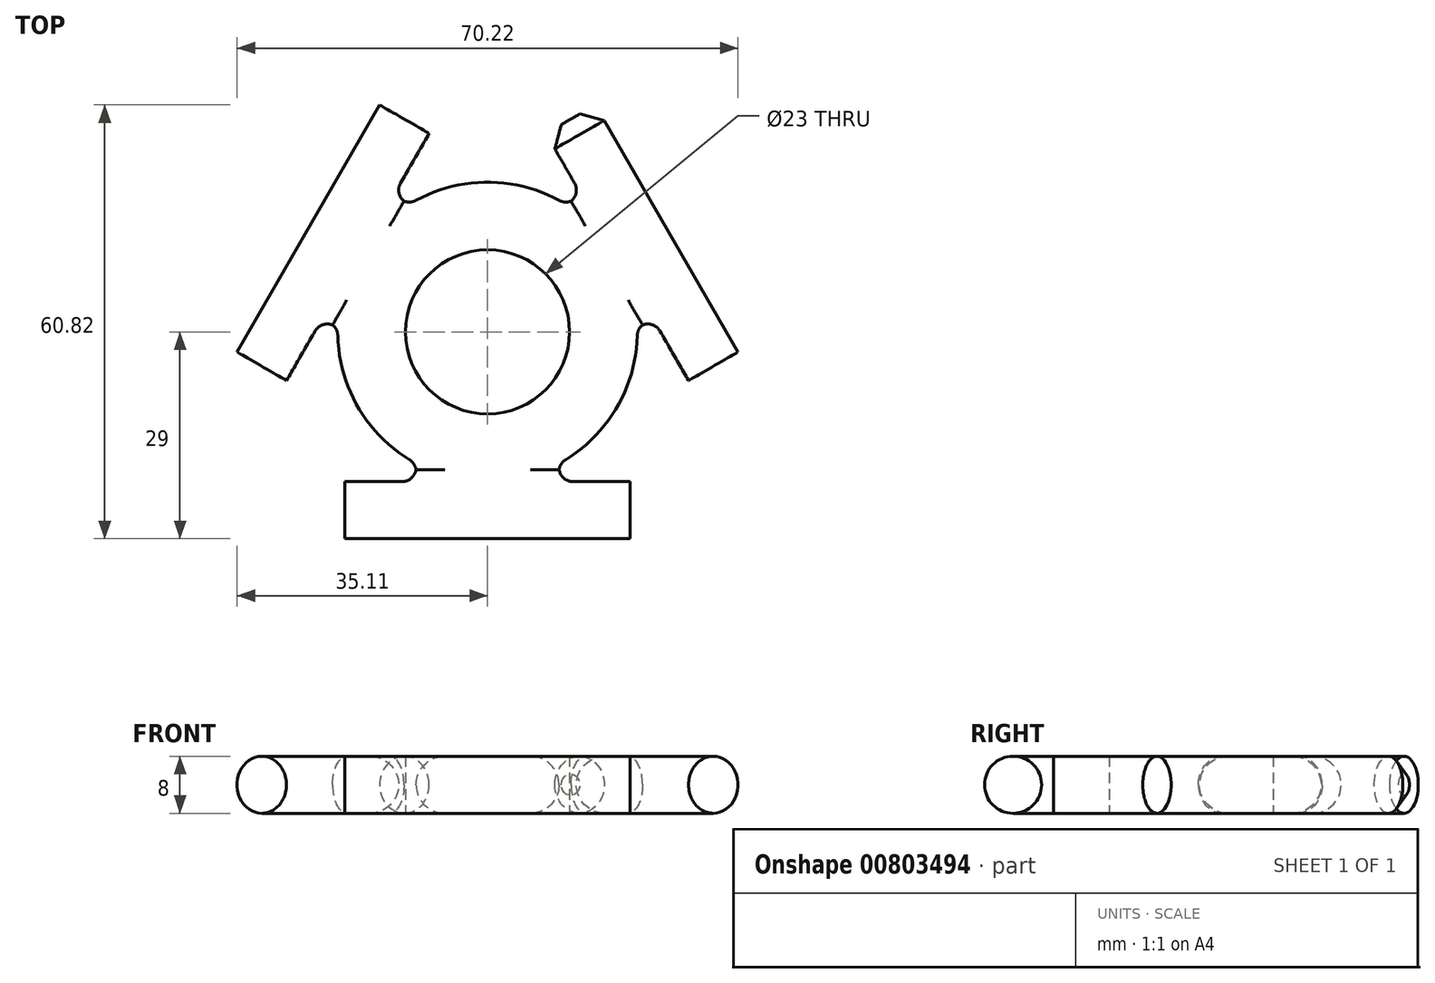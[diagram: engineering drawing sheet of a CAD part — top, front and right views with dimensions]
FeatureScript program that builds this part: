
annotation { "Feature Type Name" : "Feature", "Feature Type Description" : "" }
export const myFeature = defineFeature(function(context is Context, id is Id, definition is map)
    precondition{}
    {
        {
            var Q0;
            Q0=qCreatedBy(makeId("Top.planeOp"),FACE);
            var sketch = newSketch(context, id + "F0", { "sketchPlane" : qUnion([Q0])});
            skLineSegment(sketch, "E0", {"start": v(0, 45.61) * mm, "end": v(0, -48.73) * mm, "construction": true});
            skLineSegment(sketch, "E1", {"start": v(0, -21) * mm, "end": v(-20, -21) * mm});
            skLineSegment(sketch, "E2", {"start": v(-20, -21) * mm, "end": v(-20, -29) * mm});
            skLineSegment(sketch, "E3", {"start": v(-20, -29) * mm, "end": v(0, -29) * mm});
            skLineSegment(sketch, "E4", {"start": v(-20, -25) * mm, "end": v(0, -25) * mm, "construction": true});
            skCircle(sketch, "E5", {"center": v(0, 0) * mm, "radius": 11.5 * mm});
            skCircle(sketch, "E6", {"center": v(0, 0) * mm, "radius": 21 * mm});
            skLineSegment(sketch, "E7.MirrorCS", {"start": v(0, -21) * mm, "end": v(20, -21) * mm});
            skLineSegment(sketch, "E8.MirrorCS", {"start": v(20, -21) * mm, "end": v(20, -29) * mm});
            skLineSegment(sketch, "E9.MirrorCS", {"start": v(20, -29) * mm, "end": v(0, -29) * mm});
            skLineSegment(sketch, "E10", {"start": v(0, 0) * mm, "end": v(46.84, 27.05) * mm, "construction": true});
            skLineSegment(sketch, "E11", {"start": v(0, 0) * mm, "end": v(-46.66, 26.94) * mm, "construction": true});
            skLineSegment(sketch, "E12.1.0", {"start": v(18.19, 10.5) * mm, "end": v(28.19, -6.82) * mm});
            skLineSegment(sketch, "E12.1.1", {"start": v(28.19, -6.82) * mm, "end": v(35.11, -2.82) * mm});
            skLineSegment(sketch, "E12.1.2", {"start": v(35.11, -2.82) * mm, "end": v(25.11, 14.5) * mm});
            skLineSegment(sketch, "E12.1.3", {"start": v(15.11, 31.82) * mm, "end": v(25.11, 14.5) * mm});
            skLineSegment(sketch, "E12.1.4", {"start": v(8.19, 27.82) * mm, "end": v(15.11, 31.82) * mm});
            skLineSegment(sketch, "E12.1.5", {"start": v(18.19, 10.5) * mm, "end": v(8.19, 27.82) * mm});
            skLineSegment(sketch, "E12.2.0", {"start": v(-18.19, 10.5) * mm, "end": v(-8.19, 27.82) * mm});
            skLineSegment(sketch, "E12.2.1", {"start": v(-8.19, 27.82) * mm, "end": v(-15.11, 31.82) * mm});
            skLineSegment(sketch, "E12.2.2", {"start": v(-15.11, 31.82) * mm, "end": v(-25.11, 14.5) * mm});
            skLineSegment(sketch, "E12.2.3", {"start": v(-35.11, -2.82) * mm, "end": v(-25.11, 14.5) * mm});
            skLineSegment(sketch, "E12.2.4", {"start": v(-28.19, -6.82) * mm, "end": v(-35.11, -2.82) * mm});
            skLineSegment(sketch, "E12.2.5", {"start": v(-18.19, 10.5) * mm, "end": v(-28.19, -6.82) * mm});
            skLineSegment(sketch, "E13", {"start": v(-10, -21) * mm, "end": v(-10, -18.47) * mm});
            skLineSegment(sketch, "E14", {"start": v(10, -21) * mm, "end": v(10, -18.47) * mm});
            skLineSegment(sketch, "E15.1.0", {"start": v(13.19, 19.16) * mm, "end": v(11, 17.9) * mm});
            skLineSegment(sketch, "E15.1.1", {"start": v(23.19, 1.84) * mm, "end": v(21, 0.57) * mm});
            skLineSegment(sketch, "E15.2.0", {"start": v(-23.19, 1.84) * mm, "end": v(-21, 0.57) * mm});
            skLineSegment(sketch, "E15.2.1", {"start": v(-13.19, 19.16) * mm, "end": v(-11, 17.9) * mm});
            skSolve(sketch);
        }
        {
            var Q0;
            Q0 = qSketchRegion(id + "F0", true);
            extrude(context, id + "F1", {"entities" : qUnion([Q0]), "depth" : 8 * mm, "offsetDistance" : 25 * mm});
        }
        {
            var Q0;
            Q0=makeQuery(id+"F1.opExtrude","SWEPT_EDGE",EDGE,{"disambiguationData":[OSD([sQuery(id+"F0.wireOp",EDGE,"E6"),sQuery(id+"F0.wireOp",EDGE,"E15.2.1")])]});
            var Q1;
            Q1=makeQuery(id+"F1.opExtrude","SWEPT_EDGE",EDGE,{"disambiguationData":[OSD([sQuery(id+"F0.wireOp",EDGE,"E6"),sQuery(id+"F0.wireOp",EDGE,"E15.1.0")])]});
            var Q2;
            Q2=makeQuery(id+"F1.opExtrude","SWEPT_EDGE",EDGE,{"disambiguationData":[OSD([sQuery(id+"F0.wireOp",EDGE,"E12.1.5"),sQuery(id+"F0.wireOp",EDGE,"E15.1.0")])]});
            var Q3;
            Q3=makeQuery(id+"F1.opExtrude","SWEPT_EDGE",EDGE,{"disambiguationData":[OSD([sQuery(id+"F0.wireOp",EDGE,"E12.2.0"),sQuery(id+"F0.wireOp",EDGE,"E15.2.1")])]});
            var Q4;
            Q4=makeQuery(id+"F1.opExtrude","SWEPT_EDGE",EDGE,{"disambiguationData":[OSD([sQuery(id+"F0.wireOp",EDGE,"E6"),sQuery(id+"F0.wireOp",EDGE,"E15.1.1")])]});
            var Q5;
            Q5=makeQuery(id+"F1.opExtrude","SWEPT_EDGE",EDGE,{"disambiguationData":[OSD([sQuery(id+"F0.wireOp",EDGE,"E6"),sQuery(id+"F0.wireOp",EDGE,"E14")])]});
            var Q6;
            Q6=makeQuery(id+"F1.opExtrude","SWEPT_EDGE",EDGE,{"disambiguationData":[OSD([sQuery(id+"F0.wireOp",EDGE,"E12.1.0"),sQuery(id+"F0.wireOp",EDGE,"E15.1.1")])]});
            var Q7;
            Q7=makeQuery(id+"F1.opExtrude","SWEPT_EDGE",EDGE,{"disambiguationData":[OSD([sQuery(id+"F0.wireOp",EDGE,"E7.MirrorCS"),sQuery(id+"F0.wireOp",EDGE,"E14")])]});
            var Q8;
            Q8=makeQuery(id+"F1.opExtrude","SWEPT_EDGE",EDGE,{"disambiguationData":[OSD([sQuery(id+"F0.wireOp",EDGE,"E12.2.5"),sQuery(id+"F0.wireOp",EDGE,"E15.2.0")])]});
            var Q9;
            Q9=makeQuery(id+"F1.opExtrude","SWEPT_EDGE",EDGE,{"disambiguationData":[OSD([sQuery(id+"F0.wireOp",EDGE,"E6"),sQuery(id+"F0.wireOp",EDGE,"E15.2.0")])]});
            var Q10;
            Q10=makeQuery(id+"F1.opExtrude","SWEPT_EDGE",EDGE,{"disambiguationData":[OSD([sQuery(id+"F0.wireOp",EDGE,"E6"),sQuery(id+"F0.wireOp",EDGE,"E13")])]});
            var Q11;
            Q11=makeQuery(id+"F1.opExtrude","SWEPT_EDGE",EDGE,{"disambiguationData":[OSD([sQuery(id+"F0.wireOp",EDGE,"E1"),sQuery(id+"F0.wireOp",EDGE,"E13")])]});
            fillet(context, id + "F2", {"entities" : qUnion([Q0, Q1, Q2, Q3, Q4, Q5, Q6, Q7, Q8, Q9, Q10, Q11]), "radius" : 2 * mm, "tangentPropagation" : true, "allowEdgeOverflow" : false});
        }
        {
            var Q0;
            Q0=makeQuery(id+"F1.opExtrude","CAP_EDGE",EDGE,{"disambiguationData":[OSD([sQuery(id+"F0.wireOp",EDGE,"E3"),sQuery(id+"F0.wireOp",EDGE,"E9.MirrorCS")])],"isStart":false});
            var Q1;
            Q1=makeQuery(id+"F1.opExtrude","CAP_EDGE",EDGE,{"disambiguationData":[OSD([sQuery(id+"F0.wireOp",EDGE,"E1")])],"isStart":false});
            var Q2;
            {var subQ0=sQuery(id+"F0.wireOp",EDGE,"E13");var subQ1=sQuery(id+"F0.wireOp",EDGE,"E1");Q2=makeQuery(id+"F2.opFillet","BLEND_EDGE",EDGE,{"blendedFrom":[makeQuery(id+"F1.opExtrude","SWEPT_EDGE",EDGE,{"disambiguationData":[OSD([subQ1,subQ0])]}),makeQuery(id+"F1.opExtrude","CAP_FACE",FACE,{"disambiguationData":[OSD([subQ1,sQuery(id+"F0.wireOp",EDGE,"E2"),sQuery(id+"F0.wireOp",EDGE,"E3"),sQuery(id+"F0.wireOp",EDGE,"E5"),sQuery(id+"F0.wireOp",EDGE,"E6"),sQuery(id+"F0.wireOp",EDGE,"E7.MirrorCS"),sQuery(id+"F0.wireOp",EDGE,"E8.MirrorCS"),sQuery(id+"F0.wireOp",EDGE,"E9.MirrorCS"),sQuery(id+"F0.wireOp",EDGE,"E12.1.0"),sQuery(id+"F0.wireOp",EDGE,"E12.1.1"),sQuery(id+"F0.wireOp",EDGE,"E12.1.2"),sQuery(id+"F0.wireOp",EDGE,"E12.1.3"),sQuery(id+"F0.wireOp",EDGE,"E12.1.4"),sQuery(id+"F0.wireOp",EDGE,"E12.1.5"),sQuery(id+"F0.wireOp",EDGE,"E12.2.0"),sQuery(id+"F0.wireOp",EDGE,"E12.2.1"),sQuery(id+"F0.wireOp",EDGE,"E12.2.2"),sQuery(id+"F0.wireOp",EDGE,"E12.2.3"),sQuery(id+"F0.wireOp",EDGE,"E12.2.4"),sQuery(id+"F0.wireOp",EDGE,"E12.2.5"),subQ0,sQuery(id+"F0.wireOp",EDGE,"E14"),sQuery(id+"F0.wireOp",EDGE,"E15.1.0"),sQuery(id+"F0.wireOp",EDGE,"E15.1.1"),sQuery(id+"F0.wireOp",EDGE,"E15.2.0"),sQuery(id+"F0.wireOp",EDGE,"E15.2.1")])],"isStart":false})],"blendedInto":[makeQuery(id+"F1.opExtrude","CAP_FACE",FACE,{"disambiguationData":[OSD([subQ1,sQuery(id+"F0.wireOp",EDGE,"E2"),sQuery(id+"F0.wireOp",EDGE,"E3"),sQuery(id+"F0.wireOp",EDGE,"E5"),sQuery(id+"F0.wireOp",EDGE,"E6"),sQuery(id+"F0.wireOp",EDGE,"E7.MirrorCS"),sQuery(id+"F0.wireOp",EDGE,"E8.MirrorCS"),sQuery(id+"F0.wireOp",EDGE,"E9.MirrorCS"),sQuery(id+"F0.wireOp",EDGE,"E12.1.0"),sQuery(id+"F0.wireOp",EDGE,"E12.1.1"),sQuery(id+"F0.wireOp",EDGE,"E12.1.2"),sQuery(id+"F0.wireOp",EDGE,"E12.1.3"),sQuery(id+"F0.wireOp",EDGE,"E12.1.4"),sQuery(id+"F0.wireOp",EDGE,"E12.1.5"),sQuery(id+"F0.wireOp",EDGE,"E12.2.0"),sQuery(id+"F0.wireOp",EDGE,"E12.2.1"),sQuery(id+"F0.wireOp",EDGE,"E12.2.2"),sQuery(id+"F0.wireOp",EDGE,"E12.2.3"),sQuery(id+"F0.wireOp",EDGE,"E12.2.4"),sQuery(id+"F0.wireOp",EDGE,"E12.2.5"),subQ0,sQuery(id+"F0.wireOp",EDGE,"E14"),sQuery(id+"F0.wireOp",EDGE,"E15.1.0"),sQuery(id+"F0.wireOp",EDGE,"E15.1.1"),sQuery(id+"F0.wireOp",EDGE,"E15.2.0"),sQuery(id+"F0.wireOp",EDGE,"E15.2.1")])],"isStart":false})]});}
            var Q3;
            {var subQ0=sQuery(id+"F0.wireOp",EDGE,"E13");var subQ1=sQuery(id+"F0.wireOp",EDGE,"E6");Q3=makeQuery(id+"F2.opFillet","BLEND_EDGE",EDGE,{"blendedFrom":[makeQuery(id+"F1.opExtrude","SWEPT_EDGE",EDGE,{"disambiguationData":[OSD([subQ1,subQ0])]}),makeQuery(id+"F1.opExtrude","CAP_FACE",FACE,{"disambiguationData":[OSD([sQuery(id+"F0.wireOp",EDGE,"E1"),sQuery(id+"F0.wireOp",EDGE,"E2"),sQuery(id+"F0.wireOp",EDGE,"E3"),sQuery(id+"F0.wireOp",EDGE,"E5"),subQ1,sQuery(id+"F0.wireOp",EDGE,"E7.MirrorCS"),sQuery(id+"F0.wireOp",EDGE,"E8.MirrorCS"),sQuery(id+"F0.wireOp",EDGE,"E9.MirrorCS"),sQuery(id+"F0.wireOp",EDGE,"E12.1.0"),sQuery(id+"F0.wireOp",EDGE,"E12.1.1"),sQuery(id+"F0.wireOp",EDGE,"E12.1.2"),sQuery(id+"F0.wireOp",EDGE,"E12.1.3"),sQuery(id+"F0.wireOp",EDGE,"E12.1.4"),sQuery(id+"F0.wireOp",EDGE,"E12.1.5"),sQuery(id+"F0.wireOp",EDGE,"E12.2.0"),sQuery(id+"F0.wireOp",EDGE,"E12.2.1"),sQuery(id+"F0.wireOp",EDGE,"E12.2.2"),sQuery(id+"F0.wireOp",EDGE,"E12.2.3"),sQuery(id+"F0.wireOp",EDGE,"E12.2.4"),sQuery(id+"F0.wireOp",EDGE,"E12.2.5"),subQ0,sQuery(id+"F0.wireOp",EDGE,"E14"),sQuery(id+"F0.wireOp",EDGE,"E15.1.0"),sQuery(id+"F0.wireOp",EDGE,"E15.1.1"),sQuery(id+"F0.wireOp",EDGE,"E15.2.0"),sQuery(id+"F0.wireOp",EDGE,"E15.2.1")])],"isStart":false})],"blendedInto":[makeQuery(id+"F1.opExtrude","CAP_FACE",FACE,{"disambiguationData":[OSD([sQuery(id+"F0.wireOp",EDGE,"E1"),sQuery(id+"F0.wireOp",EDGE,"E2"),sQuery(id+"F0.wireOp",EDGE,"E3"),sQuery(id+"F0.wireOp",EDGE,"E5"),subQ1,sQuery(id+"F0.wireOp",EDGE,"E7.MirrorCS"),sQuery(id+"F0.wireOp",EDGE,"E8.MirrorCS"),sQuery(id+"F0.wireOp",EDGE,"E9.MirrorCS"),sQuery(id+"F0.wireOp",EDGE,"E12.1.0"),sQuery(id+"F0.wireOp",EDGE,"E12.1.1"),sQuery(id+"F0.wireOp",EDGE,"E12.1.2"),sQuery(id+"F0.wireOp",EDGE,"E12.1.3"),sQuery(id+"F0.wireOp",EDGE,"E12.1.4"),sQuery(id+"F0.wireOp",EDGE,"E12.1.5"),sQuery(id+"F0.wireOp",EDGE,"E12.2.0"),sQuery(id+"F0.wireOp",EDGE,"E12.2.1"),sQuery(id+"F0.wireOp",EDGE,"E12.2.2"),sQuery(id+"F0.wireOp",EDGE,"E12.2.3"),sQuery(id+"F0.wireOp",EDGE,"E12.2.4"),sQuery(id+"F0.wireOp",EDGE,"E12.2.5"),subQ0,sQuery(id+"F0.wireOp",EDGE,"E14"),sQuery(id+"F0.wireOp",EDGE,"E15.1.0"),sQuery(id+"F0.wireOp",EDGE,"E15.1.1"),sQuery(id+"F0.wireOp",EDGE,"E15.2.0"),sQuery(id+"F0.wireOp",EDGE,"E15.2.1")])],"isStart":false})]});}
            var Q4;
            {var subQ0=sQuery(id+"F0.wireOp",EDGE,"E6");Q4=makeQuery(id+"F1.opExtrude","CAP_EDGE",EDGE,{"disambiguationData":[OSD([subQ0]),TDD([makeQuery(id+"F0.imprint","IMPRINT",EDGE,{"disambiguationData":[TD([[makeQuery(id+"F0.imprint","INTERSECT",VERTEX,{"derivedFrom":[subQ0,sQuery(id+"F0.wireOp",EDGE,"E13")]}),1.0]])],"derivedFrom":subQ0})])],"isStart":false});}
            var Q5;
            {var subQ0=sQuery(id+"F0.wireOp",EDGE,"E15.2.0");var subQ1=sQuery(id+"F0.wireOp",EDGE,"E6");Q5=makeQuery(id+"F2.opFillet","BLEND_EDGE",EDGE,{"blendedFrom":[makeQuery(id+"F1.opExtrude","SWEPT_EDGE",EDGE,{"disambiguationData":[OSD([subQ1,subQ0])]}),makeQuery(id+"F1.opExtrude","CAP_FACE",FACE,{"disambiguationData":[OSD([sQuery(id+"F0.wireOp",EDGE,"E1"),sQuery(id+"F0.wireOp",EDGE,"E2"),sQuery(id+"F0.wireOp",EDGE,"E3"),sQuery(id+"F0.wireOp",EDGE,"E5"),subQ1,sQuery(id+"F0.wireOp",EDGE,"E7.MirrorCS"),sQuery(id+"F0.wireOp",EDGE,"E8.MirrorCS"),sQuery(id+"F0.wireOp",EDGE,"E9.MirrorCS"),sQuery(id+"F0.wireOp",EDGE,"E12.1.0"),sQuery(id+"F0.wireOp",EDGE,"E12.1.1"),sQuery(id+"F0.wireOp",EDGE,"E12.1.2"),sQuery(id+"F0.wireOp",EDGE,"E12.1.3"),sQuery(id+"F0.wireOp",EDGE,"E12.1.4"),sQuery(id+"F0.wireOp",EDGE,"E12.1.5"),sQuery(id+"F0.wireOp",EDGE,"E12.2.0"),sQuery(id+"F0.wireOp",EDGE,"E12.2.1"),sQuery(id+"F0.wireOp",EDGE,"E12.2.2"),sQuery(id+"F0.wireOp",EDGE,"E12.2.3"),sQuery(id+"F0.wireOp",EDGE,"E12.2.4"),sQuery(id+"F0.wireOp",EDGE,"E12.2.5"),sQuery(id+"F0.wireOp",EDGE,"E13"),sQuery(id+"F0.wireOp",EDGE,"E14"),sQuery(id+"F0.wireOp",EDGE,"E15.1.0"),sQuery(id+"F0.wireOp",EDGE,"E15.1.1"),subQ0,sQuery(id+"F0.wireOp",EDGE,"E15.2.1")])],"isStart":false})],"blendedInto":[makeQuery(id+"F1.opExtrude","CAP_FACE",FACE,{"disambiguationData":[OSD([sQuery(id+"F0.wireOp",EDGE,"E1"),sQuery(id+"F0.wireOp",EDGE,"E2"),sQuery(id+"F0.wireOp",EDGE,"E3"),sQuery(id+"F0.wireOp",EDGE,"E5"),subQ1,sQuery(id+"F0.wireOp",EDGE,"E7.MirrorCS"),sQuery(id+"F0.wireOp",EDGE,"E8.MirrorCS"),sQuery(id+"F0.wireOp",EDGE,"E9.MirrorCS"),sQuery(id+"F0.wireOp",EDGE,"E12.1.0"),sQuery(id+"F0.wireOp",EDGE,"E12.1.1"),sQuery(id+"F0.wireOp",EDGE,"E12.1.2"),sQuery(id+"F0.wireOp",EDGE,"E12.1.3"),sQuery(id+"F0.wireOp",EDGE,"E12.1.4"),sQuery(id+"F0.wireOp",EDGE,"E12.1.5"),sQuery(id+"F0.wireOp",EDGE,"E12.2.0"),sQuery(id+"F0.wireOp",EDGE,"E12.2.1"),sQuery(id+"F0.wireOp",EDGE,"E12.2.2"),sQuery(id+"F0.wireOp",EDGE,"E12.2.3"),sQuery(id+"F0.wireOp",EDGE,"E12.2.4"),sQuery(id+"F0.wireOp",EDGE,"E12.2.5"),sQuery(id+"F0.wireOp",EDGE,"E13"),sQuery(id+"F0.wireOp",EDGE,"E14"),sQuery(id+"F0.wireOp",EDGE,"E15.1.0"),sQuery(id+"F0.wireOp",EDGE,"E15.1.1"),subQ0,sQuery(id+"F0.wireOp",EDGE,"E15.2.1")])],"isStart":false})]});}
            var Q6;
            {var subQ0=sQuery(id+"F0.wireOp",EDGE,"E15.2.0");var subQ1=sQuery(id+"F0.wireOp",EDGE,"E12.2.5");Q6=makeQuery(id+"F2.opFillet","BLEND_EDGE",EDGE,{"blendedFrom":[makeQuery(id+"F1.opExtrude","SWEPT_EDGE",EDGE,{"disambiguationData":[OSD([subQ1,subQ0])]}),makeQuery(id+"F1.opExtrude","CAP_FACE",FACE,{"disambiguationData":[OSD([sQuery(id+"F0.wireOp",EDGE,"E1"),sQuery(id+"F0.wireOp",EDGE,"E2"),sQuery(id+"F0.wireOp",EDGE,"E3"),sQuery(id+"F0.wireOp",EDGE,"E5"),sQuery(id+"F0.wireOp",EDGE,"E6"),sQuery(id+"F0.wireOp",EDGE,"E7.MirrorCS"),sQuery(id+"F0.wireOp",EDGE,"E8.MirrorCS"),sQuery(id+"F0.wireOp",EDGE,"E9.MirrorCS"),sQuery(id+"F0.wireOp",EDGE,"E12.1.0"),sQuery(id+"F0.wireOp",EDGE,"E12.1.1"),sQuery(id+"F0.wireOp",EDGE,"E12.1.2"),sQuery(id+"F0.wireOp",EDGE,"E12.1.3"),sQuery(id+"F0.wireOp",EDGE,"E12.1.4"),sQuery(id+"F0.wireOp",EDGE,"E12.1.5"),sQuery(id+"F0.wireOp",EDGE,"E12.2.0"),sQuery(id+"F0.wireOp",EDGE,"E12.2.1"),sQuery(id+"F0.wireOp",EDGE,"E12.2.2"),sQuery(id+"F0.wireOp",EDGE,"E12.2.3"),sQuery(id+"F0.wireOp",EDGE,"E12.2.4"),subQ1,sQuery(id+"F0.wireOp",EDGE,"E13"),sQuery(id+"F0.wireOp",EDGE,"E14"),sQuery(id+"F0.wireOp",EDGE,"E15.1.0"),sQuery(id+"F0.wireOp",EDGE,"E15.1.1"),subQ0,sQuery(id+"F0.wireOp",EDGE,"E15.2.1")])],"isStart":false})],"blendedInto":[makeQuery(id+"F1.opExtrude","CAP_FACE",FACE,{"disambiguationData":[OSD([sQuery(id+"F0.wireOp",EDGE,"E1"),sQuery(id+"F0.wireOp",EDGE,"E2"),sQuery(id+"F0.wireOp",EDGE,"E3"),sQuery(id+"F0.wireOp",EDGE,"E5"),sQuery(id+"F0.wireOp",EDGE,"E6"),sQuery(id+"F0.wireOp",EDGE,"E7.MirrorCS"),sQuery(id+"F0.wireOp",EDGE,"E8.MirrorCS"),sQuery(id+"F0.wireOp",EDGE,"E9.MirrorCS"),sQuery(id+"F0.wireOp",EDGE,"E12.1.0"),sQuery(id+"F0.wireOp",EDGE,"E12.1.1"),sQuery(id+"F0.wireOp",EDGE,"E12.1.2"),sQuery(id+"F0.wireOp",EDGE,"E12.1.3"),sQuery(id+"F0.wireOp",EDGE,"E12.1.4"),sQuery(id+"F0.wireOp",EDGE,"E12.1.5"),sQuery(id+"F0.wireOp",EDGE,"E12.2.0"),sQuery(id+"F0.wireOp",EDGE,"E12.2.1"),sQuery(id+"F0.wireOp",EDGE,"E12.2.2"),sQuery(id+"F0.wireOp",EDGE,"E12.2.3"),sQuery(id+"F0.wireOp",EDGE,"E12.2.4"),subQ1,sQuery(id+"F0.wireOp",EDGE,"E13"),sQuery(id+"F0.wireOp",EDGE,"E14"),sQuery(id+"F0.wireOp",EDGE,"E15.1.0"),sQuery(id+"F0.wireOp",EDGE,"E15.1.1"),subQ0,sQuery(id+"F0.wireOp",EDGE,"E15.2.1")])],"isStart":false})]});}
            var Q7;
            Q7=makeQuery(id+"F1.opExtrude","CAP_EDGE",EDGE,{"disambiguationData":[OSD([sQuery(id+"F0.wireOp",EDGE,"E12.2.5")])],"isStart":false});
            var Q8;
            Q8=makeQuery(id+"F1.opExtrude","CAP_EDGE",EDGE,{"disambiguationData":[OSD([sQuery(id+"F0.wireOp",EDGE,"E7.MirrorCS")])],"isStart":false});
            var Q9;
            {var subQ0=sQuery(id+"F0.wireOp",EDGE,"E6");Q9=makeQuery(id+"F1.opExtrude","CAP_EDGE",EDGE,{"disambiguationData":[OSD([subQ0]),TDD([makeQuery(id+"F0.imprint","IMPRINT",EDGE,{"disambiguationData":[TD([[makeQuery(id+"F0.imprint","INTERSECT",VERTEX,{"derivedFrom":[subQ0,sQuery(id+"F0.wireOp",EDGE,"E14")]}),-1.0]])],"derivedFrom":subQ0})])],"isStart":false});}
            var Q10;
            {var subQ0=sQuery(id+"F0.wireOp",EDGE,"E14");var subQ1=sQuery(id+"F0.wireOp",EDGE,"E7.MirrorCS");Q10=makeQuery(id+"F2.opFillet","BLEND_EDGE",EDGE,{"blendedFrom":[makeQuery(id+"F1.opExtrude","SWEPT_EDGE",EDGE,{"disambiguationData":[OSD([subQ1,subQ0])]}),makeQuery(id+"F1.opExtrude","CAP_FACE",FACE,{"disambiguationData":[OSD([sQuery(id+"F0.wireOp",EDGE,"E1"),sQuery(id+"F0.wireOp",EDGE,"E2"),sQuery(id+"F0.wireOp",EDGE,"E3"),sQuery(id+"F0.wireOp",EDGE,"E5"),sQuery(id+"F0.wireOp",EDGE,"E6"),subQ1,sQuery(id+"F0.wireOp",EDGE,"E8.MirrorCS"),sQuery(id+"F0.wireOp",EDGE,"E9.MirrorCS"),sQuery(id+"F0.wireOp",EDGE,"E12.1.0"),sQuery(id+"F0.wireOp",EDGE,"E12.1.1"),sQuery(id+"F0.wireOp",EDGE,"E12.1.2"),sQuery(id+"F0.wireOp",EDGE,"E12.1.3"),sQuery(id+"F0.wireOp",EDGE,"E12.1.4"),sQuery(id+"F0.wireOp",EDGE,"E12.1.5"),sQuery(id+"F0.wireOp",EDGE,"E12.2.0"),sQuery(id+"F0.wireOp",EDGE,"E12.2.1"),sQuery(id+"F0.wireOp",EDGE,"E12.2.2"),sQuery(id+"F0.wireOp",EDGE,"E12.2.3"),sQuery(id+"F0.wireOp",EDGE,"E12.2.4"),sQuery(id+"F0.wireOp",EDGE,"E12.2.5"),sQuery(id+"F0.wireOp",EDGE,"E13"),subQ0,sQuery(id+"F0.wireOp",EDGE,"E15.1.0"),sQuery(id+"F0.wireOp",EDGE,"E15.1.1"),sQuery(id+"F0.wireOp",EDGE,"E15.2.0"),sQuery(id+"F0.wireOp",EDGE,"E15.2.1")])],"isStart":false})],"blendedInto":[makeQuery(id+"F1.opExtrude","CAP_FACE",FACE,{"disambiguationData":[OSD([sQuery(id+"F0.wireOp",EDGE,"E1"),sQuery(id+"F0.wireOp",EDGE,"E2"),sQuery(id+"F0.wireOp",EDGE,"E3"),sQuery(id+"F0.wireOp",EDGE,"E5"),sQuery(id+"F0.wireOp",EDGE,"E6"),subQ1,sQuery(id+"F0.wireOp",EDGE,"E8.MirrorCS"),sQuery(id+"F0.wireOp",EDGE,"E9.MirrorCS"),sQuery(id+"F0.wireOp",EDGE,"E12.1.0"),sQuery(id+"F0.wireOp",EDGE,"E12.1.1"),sQuery(id+"F0.wireOp",EDGE,"E12.1.2"),sQuery(id+"F0.wireOp",EDGE,"E12.1.3"),sQuery(id+"F0.wireOp",EDGE,"E12.1.4"),sQuery(id+"F0.wireOp",EDGE,"E12.1.5"),sQuery(id+"F0.wireOp",EDGE,"E12.2.0"),sQuery(id+"F0.wireOp",EDGE,"E12.2.1"),sQuery(id+"F0.wireOp",EDGE,"E12.2.2"),sQuery(id+"F0.wireOp",EDGE,"E12.2.3"),sQuery(id+"F0.wireOp",EDGE,"E12.2.4"),sQuery(id+"F0.wireOp",EDGE,"E12.2.5"),sQuery(id+"F0.wireOp",EDGE,"E13"),subQ0,sQuery(id+"F0.wireOp",EDGE,"E15.1.0"),sQuery(id+"F0.wireOp",EDGE,"E15.1.1"),sQuery(id+"F0.wireOp",EDGE,"E15.2.0"),sQuery(id+"F0.wireOp",EDGE,"E15.2.1")])],"isStart":false})]});}
            var Q11;
            {var subQ0=sQuery(id+"F0.wireOp",EDGE,"E14");var subQ1=sQuery(id+"F0.wireOp",EDGE,"E6");Q11=makeQuery(id+"F2.opFillet","BLEND_EDGE",EDGE,{"blendedFrom":[makeQuery(id+"F1.opExtrude","SWEPT_EDGE",EDGE,{"disambiguationData":[OSD([subQ1,subQ0])]}),makeQuery(id+"F1.opExtrude","CAP_FACE",FACE,{"disambiguationData":[OSD([sQuery(id+"F0.wireOp",EDGE,"E1"),sQuery(id+"F0.wireOp",EDGE,"E2"),sQuery(id+"F0.wireOp",EDGE,"E3"),sQuery(id+"F0.wireOp",EDGE,"E5"),subQ1,sQuery(id+"F0.wireOp",EDGE,"E7.MirrorCS"),sQuery(id+"F0.wireOp",EDGE,"E8.MirrorCS"),sQuery(id+"F0.wireOp",EDGE,"E9.MirrorCS"),sQuery(id+"F0.wireOp",EDGE,"E12.1.0"),sQuery(id+"F0.wireOp",EDGE,"E12.1.1"),sQuery(id+"F0.wireOp",EDGE,"E12.1.2"),sQuery(id+"F0.wireOp",EDGE,"E12.1.3"),sQuery(id+"F0.wireOp",EDGE,"E12.1.4"),sQuery(id+"F0.wireOp",EDGE,"E12.1.5"),sQuery(id+"F0.wireOp",EDGE,"E12.2.0"),sQuery(id+"F0.wireOp",EDGE,"E12.2.1"),sQuery(id+"F0.wireOp",EDGE,"E12.2.2"),sQuery(id+"F0.wireOp",EDGE,"E12.2.3"),sQuery(id+"F0.wireOp",EDGE,"E12.2.4"),sQuery(id+"F0.wireOp",EDGE,"E12.2.5"),sQuery(id+"F0.wireOp",EDGE,"E13"),subQ0,sQuery(id+"F0.wireOp",EDGE,"E15.1.0"),sQuery(id+"F0.wireOp",EDGE,"E15.1.1"),sQuery(id+"F0.wireOp",EDGE,"E15.2.0"),sQuery(id+"F0.wireOp",EDGE,"E15.2.1")])],"isStart":false})],"blendedInto":[makeQuery(id+"F1.opExtrude","CAP_FACE",FACE,{"disambiguationData":[OSD([sQuery(id+"F0.wireOp",EDGE,"E1"),sQuery(id+"F0.wireOp",EDGE,"E2"),sQuery(id+"F0.wireOp",EDGE,"E3"),sQuery(id+"F0.wireOp",EDGE,"E5"),subQ1,sQuery(id+"F0.wireOp",EDGE,"E7.MirrorCS"),sQuery(id+"F0.wireOp",EDGE,"E8.MirrorCS"),sQuery(id+"F0.wireOp",EDGE,"E9.MirrorCS"),sQuery(id+"F0.wireOp",EDGE,"E12.1.0"),sQuery(id+"F0.wireOp",EDGE,"E12.1.1"),sQuery(id+"F0.wireOp",EDGE,"E12.1.2"),sQuery(id+"F0.wireOp",EDGE,"E12.1.3"),sQuery(id+"F0.wireOp",EDGE,"E12.1.4"),sQuery(id+"F0.wireOp",EDGE,"E12.1.5"),sQuery(id+"F0.wireOp",EDGE,"E12.2.0"),sQuery(id+"F0.wireOp",EDGE,"E12.2.1"),sQuery(id+"F0.wireOp",EDGE,"E12.2.2"),sQuery(id+"F0.wireOp",EDGE,"E12.2.3"),sQuery(id+"F0.wireOp",EDGE,"E12.2.4"),sQuery(id+"F0.wireOp",EDGE,"E12.2.5"),sQuery(id+"F0.wireOp",EDGE,"E13"),subQ0,sQuery(id+"F0.wireOp",EDGE,"E15.1.0"),sQuery(id+"F0.wireOp",EDGE,"E15.1.1"),sQuery(id+"F0.wireOp",EDGE,"E15.2.0"),sQuery(id+"F0.wireOp",EDGE,"E15.2.1")])],"isStart":false})]});}
            var Q12;
            {var subQ0=sQuery(id+"F0.wireOp",EDGE,"E15.1.1");var subQ1=sQuery(id+"F0.wireOp",EDGE,"E6");Q12=makeQuery(id+"F2.opFillet","BLEND_EDGE",EDGE,{"blendedFrom":[makeQuery(id+"F1.opExtrude","SWEPT_EDGE",EDGE,{"disambiguationData":[OSD([subQ1,subQ0])]}),makeQuery(id+"F1.opExtrude","CAP_FACE",FACE,{"disambiguationData":[OSD([sQuery(id+"F0.wireOp",EDGE,"E1"),sQuery(id+"F0.wireOp",EDGE,"E2"),sQuery(id+"F0.wireOp",EDGE,"E3"),sQuery(id+"F0.wireOp",EDGE,"E5"),subQ1,sQuery(id+"F0.wireOp",EDGE,"E7.MirrorCS"),sQuery(id+"F0.wireOp",EDGE,"E8.MirrorCS"),sQuery(id+"F0.wireOp",EDGE,"E9.MirrorCS"),sQuery(id+"F0.wireOp",EDGE,"E12.1.0"),sQuery(id+"F0.wireOp",EDGE,"E12.1.1"),sQuery(id+"F0.wireOp",EDGE,"E12.1.2"),sQuery(id+"F0.wireOp",EDGE,"E12.1.3"),sQuery(id+"F0.wireOp",EDGE,"E12.1.4"),sQuery(id+"F0.wireOp",EDGE,"E12.1.5"),sQuery(id+"F0.wireOp",EDGE,"E12.2.0"),sQuery(id+"F0.wireOp",EDGE,"E12.2.1"),sQuery(id+"F0.wireOp",EDGE,"E12.2.2"),sQuery(id+"F0.wireOp",EDGE,"E12.2.3"),sQuery(id+"F0.wireOp",EDGE,"E12.2.4"),sQuery(id+"F0.wireOp",EDGE,"E12.2.5"),sQuery(id+"F0.wireOp",EDGE,"E13"),sQuery(id+"F0.wireOp",EDGE,"E14"),sQuery(id+"F0.wireOp",EDGE,"E15.1.0"),subQ0,sQuery(id+"F0.wireOp",EDGE,"E15.2.0"),sQuery(id+"F0.wireOp",EDGE,"E15.2.1")])],"isStart":false})],"blendedInto":[makeQuery(id+"F1.opExtrude","CAP_FACE",FACE,{"disambiguationData":[OSD([sQuery(id+"F0.wireOp",EDGE,"E1"),sQuery(id+"F0.wireOp",EDGE,"E2"),sQuery(id+"F0.wireOp",EDGE,"E3"),sQuery(id+"F0.wireOp",EDGE,"E5"),subQ1,sQuery(id+"F0.wireOp",EDGE,"E7.MirrorCS"),sQuery(id+"F0.wireOp",EDGE,"E8.MirrorCS"),sQuery(id+"F0.wireOp",EDGE,"E9.MirrorCS"),sQuery(id+"F0.wireOp",EDGE,"E12.1.0"),sQuery(id+"F0.wireOp",EDGE,"E12.1.1"),sQuery(id+"F0.wireOp",EDGE,"E12.1.2"),sQuery(id+"F0.wireOp",EDGE,"E12.1.3"),sQuery(id+"F0.wireOp",EDGE,"E12.1.4"),sQuery(id+"F0.wireOp",EDGE,"E12.1.5"),sQuery(id+"F0.wireOp",EDGE,"E12.2.0"),sQuery(id+"F0.wireOp",EDGE,"E12.2.1"),sQuery(id+"F0.wireOp",EDGE,"E12.2.2"),sQuery(id+"F0.wireOp",EDGE,"E12.2.3"),sQuery(id+"F0.wireOp",EDGE,"E12.2.4"),sQuery(id+"F0.wireOp",EDGE,"E12.2.5"),sQuery(id+"F0.wireOp",EDGE,"E13"),sQuery(id+"F0.wireOp",EDGE,"E14"),sQuery(id+"F0.wireOp",EDGE,"E15.1.0"),subQ0,sQuery(id+"F0.wireOp",EDGE,"E15.2.0"),sQuery(id+"F0.wireOp",EDGE,"E15.2.1")])],"isStart":false})]});}
            var Q13;
            {var subQ0=sQuery(id+"F0.wireOp",EDGE,"E15.1.1");var subQ1=sQuery(id+"F0.wireOp",EDGE,"E12.1.0");Q13=makeQuery(id+"F2.opFillet","BLEND_EDGE",EDGE,{"blendedFrom":[makeQuery(id+"F1.opExtrude","SWEPT_EDGE",EDGE,{"disambiguationData":[OSD([subQ1,subQ0])]}),makeQuery(id+"F1.opExtrude","CAP_FACE",FACE,{"disambiguationData":[OSD([sQuery(id+"F0.wireOp",EDGE,"E1"),sQuery(id+"F0.wireOp",EDGE,"E2"),sQuery(id+"F0.wireOp",EDGE,"E3"),sQuery(id+"F0.wireOp",EDGE,"E5"),sQuery(id+"F0.wireOp",EDGE,"E6"),sQuery(id+"F0.wireOp",EDGE,"E7.MirrorCS"),sQuery(id+"F0.wireOp",EDGE,"E8.MirrorCS"),sQuery(id+"F0.wireOp",EDGE,"E9.MirrorCS"),subQ1,sQuery(id+"F0.wireOp",EDGE,"E12.1.1"),sQuery(id+"F0.wireOp",EDGE,"E12.1.2"),sQuery(id+"F0.wireOp",EDGE,"E12.1.3"),sQuery(id+"F0.wireOp",EDGE,"E12.1.4"),sQuery(id+"F0.wireOp",EDGE,"E12.1.5"),sQuery(id+"F0.wireOp",EDGE,"E12.2.0"),sQuery(id+"F0.wireOp",EDGE,"E12.2.1"),sQuery(id+"F0.wireOp",EDGE,"E12.2.2"),sQuery(id+"F0.wireOp",EDGE,"E12.2.3"),sQuery(id+"F0.wireOp",EDGE,"E12.2.4"),sQuery(id+"F0.wireOp",EDGE,"E12.2.5"),sQuery(id+"F0.wireOp",EDGE,"E13"),sQuery(id+"F0.wireOp",EDGE,"E14"),sQuery(id+"F0.wireOp",EDGE,"E15.1.0"),subQ0,sQuery(id+"F0.wireOp",EDGE,"E15.2.0"),sQuery(id+"F0.wireOp",EDGE,"E15.2.1")])],"isStart":false})],"blendedInto":[makeQuery(id+"F1.opExtrude","CAP_FACE",FACE,{"disambiguationData":[OSD([sQuery(id+"F0.wireOp",EDGE,"E1"),sQuery(id+"F0.wireOp",EDGE,"E2"),sQuery(id+"F0.wireOp",EDGE,"E3"),sQuery(id+"F0.wireOp",EDGE,"E5"),sQuery(id+"F0.wireOp",EDGE,"E6"),sQuery(id+"F0.wireOp",EDGE,"E7.MirrorCS"),sQuery(id+"F0.wireOp",EDGE,"E8.MirrorCS"),sQuery(id+"F0.wireOp",EDGE,"E9.MirrorCS"),subQ1,sQuery(id+"F0.wireOp",EDGE,"E12.1.1"),sQuery(id+"F0.wireOp",EDGE,"E12.1.2"),sQuery(id+"F0.wireOp",EDGE,"E12.1.3"),sQuery(id+"F0.wireOp",EDGE,"E12.1.4"),sQuery(id+"F0.wireOp",EDGE,"E12.1.5"),sQuery(id+"F0.wireOp",EDGE,"E12.2.0"),sQuery(id+"F0.wireOp",EDGE,"E12.2.1"),sQuery(id+"F0.wireOp",EDGE,"E12.2.2"),sQuery(id+"F0.wireOp",EDGE,"E12.2.3"),sQuery(id+"F0.wireOp",EDGE,"E12.2.4"),sQuery(id+"F0.wireOp",EDGE,"E12.2.5"),sQuery(id+"F0.wireOp",EDGE,"E13"),sQuery(id+"F0.wireOp",EDGE,"E14"),sQuery(id+"F0.wireOp",EDGE,"E15.1.0"),subQ0,sQuery(id+"F0.wireOp",EDGE,"E15.2.0"),sQuery(id+"F0.wireOp",EDGE,"E15.2.1")])],"isStart":false})]});}
            var Q14;
            Q14=makeQuery(id+"F1.opExtrude","CAP_EDGE",EDGE,{"disambiguationData":[OSD([sQuery(id+"F0.wireOp",EDGE,"E12.2.0")])],"isStart":false});
            var Q15;
            {var subQ0=sQuery(id+"F0.wireOp",EDGE,"E6");Q15=makeQuery(id+"F1.opExtrude","CAP_EDGE",EDGE,{"disambiguationData":[OSD([subQ0]),TDD([makeQuery(id+"F0.imprint","IMPRINT",EDGE,{"disambiguationData":[TD([[makeQuery(id+"F0.imprint","INTERSECT",VERTEX,{"derivedFrom":[subQ0,sQuery(id+"F0.wireOp",EDGE,"E15.1.0")]}),-1.0]])],"derivedFrom":subQ0})])],"isStart":false});}
            var Q16;
            Q16=makeQuery(id+"F1.opExtrude","CAP_EDGE",EDGE,{"disambiguationData":[OSD([sQuery(id+"F0.wireOp",EDGE,"E12.1.5")])],"isStart":false});
            var Q17;
            Q17=makeQuery(id+"F1.opExtrude","CAP_EDGE",EDGE,{"disambiguationData":[OSD([sQuery(id+"F0.wireOp",EDGE,"E12.1.2"),sQuery(id+"F0.wireOp",EDGE,"E12.1.3")])],"isStart":false});
            var Q18;
            Q18=makeQuery(id+"F1.opExtrude","CAP_EDGE",EDGE,{"disambiguationData":[OSD([sQuery(id+"F0.wireOp",EDGE,"E12.2.2"),sQuery(id+"F0.wireOp",EDGE,"E12.2.3")])],"isStart":false});
            var Q19;
            Q19=makeQuery(id+"F1.opExtrude","CAP_EDGE",EDGE,{"disambiguationData":[OSD([sQuery(id+"F0.wireOp",EDGE,"E3"),sQuery(id+"F0.wireOp",EDGE,"E9.MirrorCS")])],"isStart":true});
            var Q20;
            {var subQ0=sQuery(id+"F0.wireOp",EDGE,"E6");Q20=makeQuery(id+"F1.opExtrude","CAP_EDGE",EDGE,{"disambiguationData":[OSD([subQ0]),TDD([makeQuery(id+"F0.imprint","IMPRINT",EDGE,{"disambiguationData":[TD([[makeQuery(id+"F0.imprint","INTERSECT",VERTEX,{"derivedFrom":[subQ0,sQuery(id+"F0.wireOp",EDGE,"E14")]}),-1.0]])],"derivedFrom":subQ0})])],"isStart":true});}
            var Q21;
            Q21=makeQuery(id+"F1.opExtrude","CAP_EDGE",EDGE,{"disambiguationData":[OSD([sQuery(id+"F0.wireOp",EDGE,"E12.1.0")])],"isStart":true});
            var Q22;
            Q22=makeQuery(id+"F1.opExtrude","CAP_EDGE",EDGE,{"disambiguationData":[OSD([sQuery(id+"F0.wireOp",EDGE,"E7.MirrorCS")])],"isStart":true});
            var Q23;
            Q23=makeQuery(id+"F1.opExtrude","CAP_EDGE",EDGE,{"disambiguationData":[OSD([sQuery(id+"F0.wireOp",EDGE,"E12.2.2"),sQuery(id+"F0.wireOp",EDGE,"E12.2.3")])],"isStart":true});
            var Q24;
            Q24=makeQuery(id+"F1.opExtrude","CAP_EDGE",EDGE,{"disambiguationData":[OSD([sQuery(id+"F0.wireOp",EDGE,"E12.1.2"),sQuery(id+"F0.wireOp",EDGE,"E12.1.3")])],"isStart":true});
            var Q25;
            Q25=makeQuery(id+"F1.opExtrude","CAP_EDGE",EDGE,{"disambiguationData":[OSD([sQuery(id+"F0.wireOp",EDGE,"E12.1.5")])],"isStart":true});
            var Q26;
            {var subQ0=sQuery(id+"F0.wireOp",EDGE,"E6");Q26=makeQuery(id+"F1.opExtrude","CAP_EDGE",EDGE,{"disambiguationData":[OSD([subQ0]),TDD([makeQuery(id+"F0.imprint","IMPRINT",EDGE,{"disambiguationData":[TD([[makeQuery(id+"F0.imprint","INTERSECT",VERTEX,{"derivedFrom":[subQ0,sQuery(id+"F0.wireOp",EDGE,"E15.1.0")]}),-1.0]])],"derivedFrom":subQ0})])],"isStart":true});}
            var Q27;
            {var subQ0=sQuery(id+"F0.wireOp",EDGE,"E6");Q27=makeQuery(id+"F1.opExtrude","CAP_EDGE",EDGE,{"disambiguationData":[OSD([subQ0]),TDD([makeQuery(id+"F0.imprint","IMPRINT",EDGE,{"disambiguationData":[TD([[makeQuery(id+"F0.imprint","INTERSECT",VERTEX,{"derivedFrom":[subQ0,sQuery(id+"F0.wireOp",EDGE,"E13")]}),1.0]])],"derivedFrom":subQ0})])],"isStart":true});}
            var Q28;
            Q28=makeQuery(id+"F1.opExtrude","CAP_EDGE",EDGE,{"disambiguationData":[OSD([sQuery(id+"F0.wireOp",EDGE,"E12.2.0")])],"isStart":true});
            var Q29;
            Q29=makeQuery(id+"F1.opExtrude","CAP_EDGE",EDGE,{"disambiguationData":[OSD([sQuery(id+"F0.wireOp",EDGE,"E12.2.5")])],"isStart":true});
            var Q30;
            {var subQ0=sQuery(id+"F0.wireOp",EDGE,"E14");var subQ1=sQuery(id+"F0.wireOp",EDGE,"E6");Q30=makeQuery(id+"F2.opFillet","BLEND_EDGE",EDGE,{"blendedFrom":[makeQuery(id+"F1.opExtrude","SWEPT_EDGE",EDGE,{"disambiguationData":[OSD([subQ1,subQ0])]}),makeQuery(id+"F1.opExtrude","CAP_FACE",FACE,{"disambiguationData":[OSD([sQuery(id+"F0.wireOp",EDGE,"E1"),sQuery(id+"F0.wireOp",EDGE,"E2"),sQuery(id+"F0.wireOp",EDGE,"E3"),sQuery(id+"F0.wireOp",EDGE,"E5"),subQ1,sQuery(id+"F0.wireOp",EDGE,"E7.MirrorCS"),sQuery(id+"F0.wireOp",EDGE,"E8.MirrorCS"),sQuery(id+"F0.wireOp",EDGE,"E9.MirrorCS"),sQuery(id+"F0.wireOp",EDGE,"E12.1.0"),sQuery(id+"F0.wireOp",EDGE,"E12.1.1"),sQuery(id+"F0.wireOp",EDGE,"E12.1.2"),sQuery(id+"F0.wireOp",EDGE,"E12.1.3"),sQuery(id+"F0.wireOp",EDGE,"E12.1.4"),sQuery(id+"F0.wireOp",EDGE,"E12.1.5"),sQuery(id+"F0.wireOp",EDGE,"E12.2.0"),sQuery(id+"F0.wireOp",EDGE,"E12.2.1"),sQuery(id+"F0.wireOp",EDGE,"E12.2.2"),sQuery(id+"F0.wireOp",EDGE,"E12.2.3"),sQuery(id+"F0.wireOp",EDGE,"E12.2.4"),sQuery(id+"F0.wireOp",EDGE,"E12.2.5"),sQuery(id+"F0.wireOp",EDGE,"E13"),subQ0,sQuery(id+"F0.wireOp",EDGE,"E15.1.0"),sQuery(id+"F0.wireOp",EDGE,"E15.1.1"),sQuery(id+"F0.wireOp",EDGE,"E15.2.0"),sQuery(id+"F0.wireOp",EDGE,"E15.2.1")])],"isStart":true})],"blendedInto":[makeQuery(id+"F1.opExtrude","CAP_FACE",FACE,{"disambiguationData":[OSD([sQuery(id+"F0.wireOp",EDGE,"E1"),sQuery(id+"F0.wireOp",EDGE,"E2"),sQuery(id+"F0.wireOp",EDGE,"E3"),sQuery(id+"F0.wireOp",EDGE,"E5"),subQ1,sQuery(id+"F0.wireOp",EDGE,"E7.MirrorCS"),sQuery(id+"F0.wireOp",EDGE,"E8.MirrorCS"),sQuery(id+"F0.wireOp",EDGE,"E9.MirrorCS"),sQuery(id+"F0.wireOp",EDGE,"E12.1.0"),sQuery(id+"F0.wireOp",EDGE,"E12.1.1"),sQuery(id+"F0.wireOp",EDGE,"E12.1.2"),sQuery(id+"F0.wireOp",EDGE,"E12.1.3"),sQuery(id+"F0.wireOp",EDGE,"E12.1.4"),sQuery(id+"F0.wireOp",EDGE,"E12.1.5"),sQuery(id+"F0.wireOp",EDGE,"E12.2.0"),sQuery(id+"F0.wireOp",EDGE,"E12.2.1"),sQuery(id+"F0.wireOp",EDGE,"E12.2.2"),sQuery(id+"F0.wireOp",EDGE,"E12.2.3"),sQuery(id+"F0.wireOp",EDGE,"E12.2.4"),sQuery(id+"F0.wireOp",EDGE,"E12.2.5"),sQuery(id+"F0.wireOp",EDGE,"E13"),subQ0,sQuery(id+"F0.wireOp",EDGE,"E15.1.0"),sQuery(id+"F0.wireOp",EDGE,"E15.1.1"),sQuery(id+"F0.wireOp",EDGE,"E15.2.0"),sQuery(id+"F0.wireOp",EDGE,"E15.2.1")])],"isStart":true})]});}
            var Q31;
            {var subQ0=sQuery(id+"F0.wireOp",EDGE,"E14");var subQ1=sQuery(id+"F0.wireOp",EDGE,"E7.MirrorCS");Q31=makeQuery(id+"F2.opFillet","BLEND_EDGE",EDGE,{"blendedFrom":[makeQuery(id+"F1.opExtrude","SWEPT_EDGE",EDGE,{"disambiguationData":[OSD([subQ1,subQ0])]}),makeQuery(id+"F1.opExtrude","CAP_FACE",FACE,{"disambiguationData":[OSD([sQuery(id+"F0.wireOp",EDGE,"E1"),sQuery(id+"F0.wireOp",EDGE,"E2"),sQuery(id+"F0.wireOp",EDGE,"E3"),sQuery(id+"F0.wireOp",EDGE,"E5"),sQuery(id+"F0.wireOp",EDGE,"E6"),subQ1,sQuery(id+"F0.wireOp",EDGE,"E8.MirrorCS"),sQuery(id+"F0.wireOp",EDGE,"E9.MirrorCS"),sQuery(id+"F0.wireOp",EDGE,"E12.1.0"),sQuery(id+"F0.wireOp",EDGE,"E12.1.1"),sQuery(id+"F0.wireOp",EDGE,"E12.1.2"),sQuery(id+"F0.wireOp",EDGE,"E12.1.3"),sQuery(id+"F0.wireOp",EDGE,"E12.1.4"),sQuery(id+"F0.wireOp",EDGE,"E12.1.5"),sQuery(id+"F0.wireOp",EDGE,"E12.2.0"),sQuery(id+"F0.wireOp",EDGE,"E12.2.1"),sQuery(id+"F0.wireOp",EDGE,"E12.2.2"),sQuery(id+"F0.wireOp",EDGE,"E12.2.3"),sQuery(id+"F0.wireOp",EDGE,"E12.2.4"),sQuery(id+"F0.wireOp",EDGE,"E12.2.5"),sQuery(id+"F0.wireOp",EDGE,"E13"),subQ0,sQuery(id+"F0.wireOp",EDGE,"E15.1.0"),sQuery(id+"F0.wireOp",EDGE,"E15.1.1"),sQuery(id+"F0.wireOp",EDGE,"E15.2.0"),sQuery(id+"F0.wireOp",EDGE,"E15.2.1")])],"isStart":true})],"blendedInto":[makeQuery(id+"F1.opExtrude","CAP_FACE",FACE,{"disambiguationData":[OSD([sQuery(id+"F0.wireOp",EDGE,"E1"),sQuery(id+"F0.wireOp",EDGE,"E2"),sQuery(id+"F0.wireOp",EDGE,"E3"),sQuery(id+"F0.wireOp",EDGE,"E5"),sQuery(id+"F0.wireOp",EDGE,"E6"),subQ1,sQuery(id+"F0.wireOp",EDGE,"E8.MirrorCS"),sQuery(id+"F0.wireOp",EDGE,"E9.MirrorCS"),sQuery(id+"F0.wireOp",EDGE,"E12.1.0"),sQuery(id+"F0.wireOp",EDGE,"E12.1.1"),sQuery(id+"F0.wireOp",EDGE,"E12.1.2"),sQuery(id+"F0.wireOp",EDGE,"E12.1.3"),sQuery(id+"F0.wireOp",EDGE,"E12.1.4"),sQuery(id+"F0.wireOp",EDGE,"E12.1.5"),sQuery(id+"F0.wireOp",EDGE,"E12.2.0"),sQuery(id+"F0.wireOp",EDGE,"E12.2.1"),sQuery(id+"F0.wireOp",EDGE,"E12.2.2"),sQuery(id+"F0.wireOp",EDGE,"E12.2.3"),sQuery(id+"F0.wireOp",EDGE,"E12.2.4"),sQuery(id+"F0.wireOp",EDGE,"E12.2.5"),sQuery(id+"F0.wireOp",EDGE,"E13"),subQ0,sQuery(id+"F0.wireOp",EDGE,"E15.1.0"),sQuery(id+"F0.wireOp",EDGE,"E15.1.1"),sQuery(id+"F0.wireOp",EDGE,"E15.2.0"),sQuery(id+"F0.wireOp",EDGE,"E15.2.1")])],"isStart":true})]});}
            var Q32;
            {var subQ0=sQuery(id+"F0.wireOp",EDGE,"E15.1.1");var subQ1=sQuery(id+"F0.wireOp",EDGE,"E12.1.0");Q32=makeQuery(id+"F2.opFillet","BLEND_EDGE",EDGE,{"blendedFrom":[makeQuery(id+"F1.opExtrude","SWEPT_EDGE",EDGE,{"disambiguationData":[OSD([subQ1,subQ0])]}),makeQuery(id+"F1.opExtrude","CAP_FACE",FACE,{"disambiguationData":[OSD([sQuery(id+"F0.wireOp",EDGE,"E1"),sQuery(id+"F0.wireOp",EDGE,"E2"),sQuery(id+"F0.wireOp",EDGE,"E3"),sQuery(id+"F0.wireOp",EDGE,"E5"),sQuery(id+"F0.wireOp",EDGE,"E6"),sQuery(id+"F0.wireOp",EDGE,"E7.MirrorCS"),sQuery(id+"F0.wireOp",EDGE,"E8.MirrorCS"),sQuery(id+"F0.wireOp",EDGE,"E9.MirrorCS"),subQ1,sQuery(id+"F0.wireOp",EDGE,"E12.1.1"),sQuery(id+"F0.wireOp",EDGE,"E12.1.2"),sQuery(id+"F0.wireOp",EDGE,"E12.1.3"),sQuery(id+"F0.wireOp",EDGE,"E12.1.4"),sQuery(id+"F0.wireOp",EDGE,"E12.1.5"),sQuery(id+"F0.wireOp",EDGE,"E12.2.0"),sQuery(id+"F0.wireOp",EDGE,"E12.2.1"),sQuery(id+"F0.wireOp",EDGE,"E12.2.2"),sQuery(id+"F0.wireOp",EDGE,"E12.2.3"),sQuery(id+"F0.wireOp",EDGE,"E12.2.4"),sQuery(id+"F0.wireOp",EDGE,"E12.2.5"),sQuery(id+"F0.wireOp",EDGE,"E13"),sQuery(id+"F0.wireOp",EDGE,"E14"),sQuery(id+"F0.wireOp",EDGE,"E15.1.0"),subQ0,sQuery(id+"F0.wireOp",EDGE,"E15.2.0"),sQuery(id+"F0.wireOp",EDGE,"E15.2.1")])],"isStart":true})],"blendedInto":[makeQuery(id+"F1.opExtrude","CAP_FACE",FACE,{"disambiguationData":[OSD([sQuery(id+"F0.wireOp",EDGE,"E1"),sQuery(id+"F0.wireOp",EDGE,"E2"),sQuery(id+"F0.wireOp",EDGE,"E3"),sQuery(id+"F0.wireOp",EDGE,"E5"),sQuery(id+"F0.wireOp",EDGE,"E6"),sQuery(id+"F0.wireOp",EDGE,"E7.MirrorCS"),sQuery(id+"F0.wireOp",EDGE,"E8.MirrorCS"),sQuery(id+"F0.wireOp",EDGE,"E9.MirrorCS"),subQ1,sQuery(id+"F0.wireOp",EDGE,"E12.1.1"),sQuery(id+"F0.wireOp",EDGE,"E12.1.2"),sQuery(id+"F0.wireOp",EDGE,"E12.1.3"),sQuery(id+"F0.wireOp",EDGE,"E12.1.4"),sQuery(id+"F0.wireOp",EDGE,"E12.1.5"),sQuery(id+"F0.wireOp",EDGE,"E12.2.0"),sQuery(id+"F0.wireOp",EDGE,"E12.2.1"),sQuery(id+"F0.wireOp",EDGE,"E12.2.2"),sQuery(id+"F0.wireOp",EDGE,"E12.2.3"),sQuery(id+"F0.wireOp",EDGE,"E12.2.4"),sQuery(id+"F0.wireOp",EDGE,"E12.2.5"),sQuery(id+"F0.wireOp",EDGE,"E13"),sQuery(id+"F0.wireOp",EDGE,"E14"),sQuery(id+"F0.wireOp",EDGE,"E15.1.0"),subQ0,sQuery(id+"F0.wireOp",EDGE,"E15.2.0"),sQuery(id+"F0.wireOp",EDGE,"E15.2.1")])],"isStart":true})]});}
            var Q33;
            {var subQ0=sQuery(id+"F0.wireOp",EDGE,"E15.1.1");var subQ1=sQuery(id+"F0.wireOp",EDGE,"E6");Q33=makeQuery(id+"F2.opFillet","BLEND_EDGE",EDGE,{"blendedFrom":[makeQuery(id+"F1.opExtrude","SWEPT_EDGE",EDGE,{"disambiguationData":[OSD([subQ1,subQ0])]}),makeQuery(id+"F1.opExtrude","CAP_FACE",FACE,{"disambiguationData":[OSD([sQuery(id+"F0.wireOp",EDGE,"E1"),sQuery(id+"F0.wireOp",EDGE,"E2"),sQuery(id+"F0.wireOp",EDGE,"E3"),sQuery(id+"F0.wireOp",EDGE,"E5"),subQ1,sQuery(id+"F0.wireOp",EDGE,"E7.MirrorCS"),sQuery(id+"F0.wireOp",EDGE,"E8.MirrorCS"),sQuery(id+"F0.wireOp",EDGE,"E9.MirrorCS"),sQuery(id+"F0.wireOp",EDGE,"E12.1.0"),sQuery(id+"F0.wireOp",EDGE,"E12.1.1"),sQuery(id+"F0.wireOp",EDGE,"E12.1.2"),sQuery(id+"F0.wireOp",EDGE,"E12.1.3"),sQuery(id+"F0.wireOp",EDGE,"E12.1.4"),sQuery(id+"F0.wireOp",EDGE,"E12.1.5"),sQuery(id+"F0.wireOp",EDGE,"E12.2.0"),sQuery(id+"F0.wireOp",EDGE,"E12.2.1"),sQuery(id+"F0.wireOp",EDGE,"E12.2.2"),sQuery(id+"F0.wireOp",EDGE,"E12.2.3"),sQuery(id+"F0.wireOp",EDGE,"E12.2.4"),sQuery(id+"F0.wireOp",EDGE,"E12.2.5"),sQuery(id+"F0.wireOp",EDGE,"E13"),sQuery(id+"F0.wireOp",EDGE,"E14"),sQuery(id+"F0.wireOp",EDGE,"E15.1.0"),subQ0,sQuery(id+"F0.wireOp",EDGE,"E15.2.0"),sQuery(id+"F0.wireOp",EDGE,"E15.2.1")])],"isStart":true})],"blendedInto":[makeQuery(id+"F1.opExtrude","CAP_FACE",FACE,{"disambiguationData":[OSD([sQuery(id+"F0.wireOp",EDGE,"E1"),sQuery(id+"F0.wireOp",EDGE,"E2"),sQuery(id+"F0.wireOp",EDGE,"E3"),sQuery(id+"F0.wireOp",EDGE,"E5"),subQ1,sQuery(id+"F0.wireOp",EDGE,"E7.MirrorCS"),sQuery(id+"F0.wireOp",EDGE,"E8.MirrorCS"),sQuery(id+"F0.wireOp",EDGE,"E9.MirrorCS"),sQuery(id+"F0.wireOp",EDGE,"E12.1.0"),sQuery(id+"F0.wireOp",EDGE,"E12.1.1"),sQuery(id+"F0.wireOp",EDGE,"E12.1.2"),sQuery(id+"F0.wireOp",EDGE,"E12.1.3"),sQuery(id+"F0.wireOp",EDGE,"E12.1.4"),sQuery(id+"F0.wireOp",EDGE,"E12.1.5"),sQuery(id+"F0.wireOp",EDGE,"E12.2.0"),sQuery(id+"F0.wireOp",EDGE,"E12.2.1"),sQuery(id+"F0.wireOp",EDGE,"E12.2.2"),sQuery(id+"F0.wireOp",EDGE,"E12.2.3"),sQuery(id+"F0.wireOp",EDGE,"E12.2.4"),sQuery(id+"F0.wireOp",EDGE,"E12.2.5"),sQuery(id+"F0.wireOp",EDGE,"E13"),sQuery(id+"F0.wireOp",EDGE,"E14"),sQuery(id+"F0.wireOp",EDGE,"E15.1.0"),subQ0,sQuery(id+"F0.wireOp",EDGE,"E15.2.0"),sQuery(id+"F0.wireOp",EDGE,"E15.2.1")])],"isStart":true})]});}
            var Q34;
            Q34=makeQuery(id+"F1.opExtrude","CAP_EDGE",EDGE,{"disambiguationData":[OSD([sQuery(id+"F0.wireOp",EDGE,"E1")])],"isStart":true});
            var Q35;
            {var subQ0=sQuery(id+"F0.wireOp",EDGE,"E13");var subQ1=sQuery(id+"F0.wireOp",EDGE,"E1");Q35=makeQuery(id+"F2.opFillet","BLEND_EDGE",EDGE,{"blendedFrom":[makeQuery(id+"F1.opExtrude","SWEPT_EDGE",EDGE,{"disambiguationData":[OSD([subQ1,subQ0])]}),makeQuery(id+"F1.opExtrude","CAP_FACE",FACE,{"disambiguationData":[OSD([subQ1,sQuery(id+"F0.wireOp",EDGE,"E2"),sQuery(id+"F0.wireOp",EDGE,"E3"),sQuery(id+"F0.wireOp",EDGE,"E5"),sQuery(id+"F0.wireOp",EDGE,"E6"),sQuery(id+"F0.wireOp",EDGE,"E7.MirrorCS"),sQuery(id+"F0.wireOp",EDGE,"E8.MirrorCS"),sQuery(id+"F0.wireOp",EDGE,"E9.MirrorCS"),sQuery(id+"F0.wireOp",EDGE,"E12.1.0"),sQuery(id+"F0.wireOp",EDGE,"E12.1.1"),sQuery(id+"F0.wireOp",EDGE,"E12.1.2"),sQuery(id+"F0.wireOp",EDGE,"E12.1.3"),sQuery(id+"F0.wireOp",EDGE,"E12.1.4"),sQuery(id+"F0.wireOp",EDGE,"E12.1.5"),sQuery(id+"F0.wireOp",EDGE,"E12.2.0"),sQuery(id+"F0.wireOp",EDGE,"E12.2.1"),sQuery(id+"F0.wireOp",EDGE,"E12.2.2"),sQuery(id+"F0.wireOp",EDGE,"E12.2.3"),sQuery(id+"F0.wireOp",EDGE,"E12.2.4"),sQuery(id+"F0.wireOp",EDGE,"E12.2.5"),subQ0,sQuery(id+"F0.wireOp",EDGE,"E14"),sQuery(id+"F0.wireOp",EDGE,"E15.1.0"),sQuery(id+"F0.wireOp",EDGE,"E15.1.1"),sQuery(id+"F0.wireOp",EDGE,"E15.2.0"),sQuery(id+"F0.wireOp",EDGE,"E15.2.1")])],"isStart":true})],"blendedInto":[makeQuery(id+"F1.opExtrude","CAP_FACE",FACE,{"disambiguationData":[OSD([subQ1,sQuery(id+"F0.wireOp",EDGE,"E2"),sQuery(id+"F0.wireOp",EDGE,"E3"),sQuery(id+"F0.wireOp",EDGE,"E5"),sQuery(id+"F0.wireOp",EDGE,"E6"),sQuery(id+"F0.wireOp",EDGE,"E7.MirrorCS"),sQuery(id+"F0.wireOp",EDGE,"E8.MirrorCS"),sQuery(id+"F0.wireOp",EDGE,"E9.MirrorCS"),sQuery(id+"F0.wireOp",EDGE,"E12.1.0"),sQuery(id+"F0.wireOp",EDGE,"E12.1.1"),sQuery(id+"F0.wireOp",EDGE,"E12.1.2"),sQuery(id+"F0.wireOp",EDGE,"E12.1.3"),sQuery(id+"F0.wireOp",EDGE,"E12.1.4"),sQuery(id+"F0.wireOp",EDGE,"E12.1.5"),sQuery(id+"F0.wireOp",EDGE,"E12.2.0"),sQuery(id+"F0.wireOp",EDGE,"E12.2.1"),sQuery(id+"F0.wireOp",EDGE,"E12.2.2"),sQuery(id+"F0.wireOp",EDGE,"E12.2.3"),sQuery(id+"F0.wireOp",EDGE,"E12.2.4"),sQuery(id+"F0.wireOp",EDGE,"E12.2.5"),subQ0,sQuery(id+"F0.wireOp",EDGE,"E14"),sQuery(id+"F0.wireOp",EDGE,"E15.1.0"),sQuery(id+"F0.wireOp",EDGE,"E15.1.1"),sQuery(id+"F0.wireOp",EDGE,"E15.2.0"),sQuery(id+"F0.wireOp",EDGE,"E15.2.1")])],"isStart":true})]});}
            var Q36;
            {var subQ0=sQuery(id+"F0.wireOp",EDGE,"E13");var subQ1=sQuery(id+"F0.wireOp",EDGE,"E6");Q36=makeQuery(id+"F2.opFillet","BLEND_EDGE",EDGE,{"blendedFrom":[makeQuery(id+"F1.opExtrude","SWEPT_EDGE",EDGE,{"disambiguationData":[OSD([subQ1,subQ0])]}),makeQuery(id+"F1.opExtrude","CAP_FACE",FACE,{"disambiguationData":[OSD([sQuery(id+"F0.wireOp",EDGE,"E1"),sQuery(id+"F0.wireOp",EDGE,"E2"),sQuery(id+"F0.wireOp",EDGE,"E3"),sQuery(id+"F0.wireOp",EDGE,"E5"),subQ1,sQuery(id+"F0.wireOp",EDGE,"E7.MirrorCS"),sQuery(id+"F0.wireOp",EDGE,"E8.MirrorCS"),sQuery(id+"F0.wireOp",EDGE,"E9.MirrorCS"),sQuery(id+"F0.wireOp",EDGE,"E12.1.0"),sQuery(id+"F0.wireOp",EDGE,"E12.1.1"),sQuery(id+"F0.wireOp",EDGE,"E12.1.2"),sQuery(id+"F0.wireOp",EDGE,"E12.1.3"),sQuery(id+"F0.wireOp",EDGE,"E12.1.4"),sQuery(id+"F0.wireOp",EDGE,"E12.1.5"),sQuery(id+"F0.wireOp",EDGE,"E12.2.0"),sQuery(id+"F0.wireOp",EDGE,"E12.2.1"),sQuery(id+"F0.wireOp",EDGE,"E12.2.2"),sQuery(id+"F0.wireOp",EDGE,"E12.2.3"),sQuery(id+"F0.wireOp",EDGE,"E12.2.4"),sQuery(id+"F0.wireOp",EDGE,"E12.2.5"),subQ0,sQuery(id+"F0.wireOp",EDGE,"E14"),sQuery(id+"F0.wireOp",EDGE,"E15.1.0"),sQuery(id+"F0.wireOp",EDGE,"E15.1.1"),sQuery(id+"F0.wireOp",EDGE,"E15.2.0"),sQuery(id+"F0.wireOp",EDGE,"E15.2.1")])],"isStart":true})],"blendedInto":[makeQuery(id+"F1.opExtrude","CAP_FACE",FACE,{"disambiguationData":[OSD([sQuery(id+"F0.wireOp",EDGE,"E1"),sQuery(id+"F0.wireOp",EDGE,"E2"),sQuery(id+"F0.wireOp",EDGE,"E3"),sQuery(id+"F0.wireOp",EDGE,"E5"),subQ1,sQuery(id+"F0.wireOp",EDGE,"E7.MirrorCS"),sQuery(id+"F0.wireOp",EDGE,"E8.MirrorCS"),sQuery(id+"F0.wireOp",EDGE,"E9.MirrorCS"),sQuery(id+"F0.wireOp",EDGE,"E12.1.0"),sQuery(id+"F0.wireOp",EDGE,"E12.1.1"),sQuery(id+"F0.wireOp",EDGE,"E12.1.2"),sQuery(id+"F0.wireOp",EDGE,"E12.1.3"),sQuery(id+"F0.wireOp",EDGE,"E12.1.4"),sQuery(id+"F0.wireOp",EDGE,"E12.1.5"),sQuery(id+"F0.wireOp",EDGE,"E12.2.0"),sQuery(id+"F0.wireOp",EDGE,"E12.2.1"),sQuery(id+"F0.wireOp",EDGE,"E12.2.2"),sQuery(id+"F0.wireOp",EDGE,"E12.2.3"),sQuery(id+"F0.wireOp",EDGE,"E12.2.4"),sQuery(id+"F0.wireOp",EDGE,"E12.2.5"),subQ0,sQuery(id+"F0.wireOp",EDGE,"E14"),sQuery(id+"F0.wireOp",EDGE,"E15.1.0"),sQuery(id+"F0.wireOp",EDGE,"E15.1.1"),sQuery(id+"F0.wireOp",EDGE,"E15.2.0"),sQuery(id+"F0.wireOp",EDGE,"E15.2.1")])],"isStart":true})]});}
            var Q37;
            {var subQ0=sQuery(id+"F0.wireOp",EDGE,"E15.2.0");var subQ1=sQuery(id+"F0.wireOp",EDGE,"E6");Q37=makeQuery(id+"F2.opFillet","BLEND_EDGE",EDGE,{"blendedFrom":[makeQuery(id+"F1.opExtrude","SWEPT_EDGE",EDGE,{"disambiguationData":[OSD([subQ1,subQ0])]}),makeQuery(id+"F1.opExtrude","CAP_FACE",FACE,{"disambiguationData":[OSD([sQuery(id+"F0.wireOp",EDGE,"E1"),sQuery(id+"F0.wireOp",EDGE,"E2"),sQuery(id+"F0.wireOp",EDGE,"E3"),sQuery(id+"F0.wireOp",EDGE,"E5"),subQ1,sQuery(id+"F0.wireOp",EDGE,"E7.MirrorCS"),sQuery(id+"F0.wireOp",EDGE,"E8.MirrorCS"),sQuery(id+"F0.wireOp",EDGE,"E9.MirrorCS"),sQuery(id+"F0.wireOp",EDGE,"E12.1.0"),sQuery(id+"F0.wireOp",EDGE,"E12.1.1"),sQuery(id+"F0.wireOp",EDGE,"E12.1.2"),sQuery(id+"F0.wireOp",EDGE,"E12.1.3"),sQuery(id+"F0.wireOp",EDGE,"E12.1.4"),sQuery(id+"F0.wireOp",EDGE,"E12.1.5"),sQuery(id+"F0.wireOp",EDGE,"E12.2.0"),sQuery(id+"F0.wireOp",EDGE,"E12.2.1"),sQuery(id+"F0.wireOp",EDGE,"E12.2.2"),sQuery(id+"F0.wireOp",EDGE,"E12.2.3"),sQuery(id+"F0.wireOp",EDGE,"E12.2.4"),sQuery(id+"F0.wireOp",EDGE,"E12.2.5"),sQuery(id+"F0.wireOp",EDGE,"E13"),sQuery(id+"F0.wireOp",EDGE,"E14"),sQuery(id+"F0.wireOp",EDGE,"E15.1.0"),sQuery(id+"F0.wireOp",EDGE,"E15.1.1"),subQ0,sQuery(id+"F0.wireOp",EDGE,"E15.2.1")])],"isStart":true})],"blendedInto":[makeQuery(id+"F1.opExtrude","CAP_FACE",FACE,{"disambiguationData":[OSD([sQuery(id+"F0.wireOp",EDGE,"E1"),sQuery(id+"F0.wireOp",EDGE,"E2"),sQuery(id+"F0.wireOp",EDGE,"E3"),sQuery(id+"F0.wireOp",EDGE,"E5"),subQ1,sQuery(id+"F0.wireOp",EDGE,"E7.MirrorCS"),sQuery(id+"F0.wireOp",EDGE,"E8.MirrorCS"),sQuery(id+"F0.wireOp",EDGE,"E9.MirrorCS"),sQuery(id+"F0.wireOp",EDGE,"E12.1.0"),sQuery(id+"F0.wireOp",EDGE,"E12.1.1"),sQuery(id+"F0.wireOp",EDGE,"E12.1.2"),sQuery(id+"F0.wireOp",EDGE,"E12.1.3"),sQuery(id+"F0.wireOp",EDGE,"E12.1.4"),sQuery(id+"F0.wireOp",EDGE,"E12.1.5"),sQuery(id+"F0.wireOp",EDGE,"E12.2.0"),sQuery(id+"F0.wireOp",EDGE,"E12.2.1"),sQuery(id+"F0.wireOp",EDGE,"E12.2.2"),sQuery(id+"F0.wireOp",EDGE,"E12.2.3"),sQuery(id+"F0.wireOp",EDGE,"E12.2.4"),sQuery(id+"F0.wireOp",EDGE,"E12.2.5"),sQuery(id+"F0.wireOp",EDGE,"E13"),sQuery(id+"F0.wireOp",EDGE,"E14"),sQuery(id+"F0.wireOp",EDGE,"E15.1.0"),sQuery(id+"F0.wireOp",EDGE,"E15.1.1"),subQ0,sQuery(id+"F0.wireOp",EDGE,"E15.2.1")])],"isStart":true})]});}
            var Q38;
            {var subQ0=sQuery(id+"F0.wireOp",EDGE,"E15.2.0");var subQ1=sQuery(id+"F0.wireOp",EDGE,"E12.2.5");Q38=makeQuery(id+"F2.opFillet","BLEND_EDGE",EDGE,{"blendedFrom":[makeQuery(id+"F1.opExtrude","SWEPT_EDGE",EDGE,{"disambiguationData":[OSD([subQ1,subQ0])]}),makeQuery(id+"F1.opExtrude","CAP_FACE",FACE,{"disambiguationData":[OSD([sQuery(id+"F0.wireOp",EDGE,"E1"),sQuery(id+"F0.wireOp",EDGE,"E2"),sQuery(id+"F0.wireOp",EDGE,"E3"),sQuery(id+"F0.wireOp",EDGE,"E5"),sQuery(id+"F0.wireOp",EDGE,"E6"),sQuery(id+"F0.wireOp",EDGE,"E7.MirrorCS"),sQuery(id+"F0.wireOp",EDGE,"E8.MirrorCS"),sQuery(id+"F0.wireOp",EDGE,"E9.MirrorCS"),sQuery(id+"F0.wireOp",EDGE,"E12.1.0"),sQuery(id+"F0.wireOp",EDGE,"E12.1.1"),sQuery(id+"F0.wireOp",EDGE,"E12.1.2"),sQuery(id+"F0.wireOp",EDGE,"E12.1.3"),sQuery(id+"F0.wireOp",EDGE,"E12.1.4"),sQuery(id+"F0.wireOp",EDGE,"E12.1.5"),sQuery(id+"F0.wireOp",EDGE,"E12.2.0"),sQuery(id+"F0.wireOp",EDGE,"E12.2.1"),sQuery(id+"F0.wireOp",EDGE,"E12.2.2"),sQuery(id+"F0.wireOp",EDGE,"E12.2.3"),sQuery(id+"F0.wireOp",EDGE,"E12.2.4"),subQ1,sQuery(id+"F0.wireOp",EDGE,"E13"),sQuery(id+"F0.wireOp",EDGE,"E14"),sQuery(id+"F0.wireOp",EDGE,"E15.1.0"),sQuery(id+"F0.wireOp",EDGE,"E15.1.1"),subQ0,sQuery(id+"F0.wireOp",EDGE,"E15.2.1")])],"isStart":true})],"blendedInto":[makeQuery(id+"F1.opExtrude","CAP_FACE",FACE,{"disambiguationData":[OSD([sQuery(id+"F0.wireOp",EDGE,"E1"),sQuery(id+"F0.wireOp",EDGE,"E2"),sQuery(id+"F0.wireOp",EDGE,"E3"),sQuery(id+"F0.wireOp",EDGE,"E5"),sQuery(id+"F0.wireOp",EDGE,"E6"),sQuery(id+"F0.wireOp",EDGE,"E7.MirrorCS"),sQuery(id+"F0.wireOp",EDGE,"E8.MirrorCS"),sQuery(id+"F0.wireOp",EDGE,"E9.MirrorCS"),sQuery(id+"F0.wireOp",EDGE,"E12.1.0"),sQuery(id+"F0.wireOp",EDGE,"E12.1.1"),sQuery(id+"F0.wireOp",EDGE,"E12.1.2"),sQuery(id+"F0.wireOp",EDGE,"E12.1.3"),sQuery(id+"F0.wireOp",EDGE,"E12.1.4"),sQuery(id+"F0.wireOp",EDGE,"E12.1.5"),sQuery(id+"F0.wireOp",EDGE,"E12.2.0"),sQuery(id+"F0.wireOp",EDGE,"E12.2.1"),sQuery(id+"F0.wireOp",EDGE,"E12.2.2"),sQuery(id+"F0.wireOp",EDGE,"E12.2.3"),sQuery(id+"F0.wireOp",EDGE,"E12.2.4"),subQ1,sQuery(id+"F0.wireOp",EDGE,"E13"),sQuery(id+"F0.wireOp",EDGE,"E14"),sQuery(id+"F0.wireOp",EDGE,"E15.1.0"),sQuery(id+"F0.wireOp",EDGE,"E15.1.1"),subQ0,sQuery(id+"F0.wireOp",EDGE,"E15.2.1")])],"isStart":true})]});}
            var Q39;
            {var subQ0=sQuery(id+"F0.wireOp",EDGE,"E15.2.1");var subQ1=sQuery(id+"F0.wireOp",EDGE,"E12.2.0");Q39=makeQuery(id+"F2.opFillet","BLEND_EDGE",EDGE,{"blendedFrom":[makeQuery(id+"F1.opExtrude","SWEPT_EDGE",EDGE,{"disambiguationData":[OSD([subQ1,subQ0])]}),makeQuery(id+"F1.opExtrude","CAP_FACE",FACE,{"disambiguationData":[OSD([sQuery(id+"F0.wireOp",EDGE,"E1"),sQuery(id+"F0.wireOp",EDGE,"E2"),sQuery(id+"F0.wireOp",EDGE,"E3"),sQuery(id+"F0.wireOp",EDGE,"E5"),sQuery(id+"F0.wireOp",EDGE,"E6"),sQuery(id+"F0.wireOp",EDGE,"E7.MirrorCS"),sQuery(id+"F0.wireOp",EDGE,"E8.MirrorCS"),sQuery(id+"F0.wireOp",EDGE,"E9.MirrorCS"),sQuery(id+"F0.wireOp",EDGE,"E12.1.0"),sQuery(id+"F0.wireOp",EDGE,"E12.1.1"),sQuery(id+"F0.wireOp",EDGE,"E12.1.2"),sQuery(id+"F0.wireOp",EDGE,"E12.1.3"),sQuery(id+"F0.wireOp",EDGE,"E12.1.4"),sQuery(id+"F0.wireOp",EDGE,"E12.1.5"),subQ1,sQuery(id+"F0.wireOp",EDGE,"E12.2.1"),sQuery(id+"F0.wireOp",EDGE,"E12.2.2"),sQuery(id+"F0.wireOp",EDGE,"E12.2.3"),sQuery(id+"F0.wireOp",EDGE,"E12.2.4"),sQuery(id+"F0.wireOp",EDGE,"E12.2.5"),sQuery(id+"F0.wireOp",EDGE,"E13"),sQuery(id+"F0.wireOp",EDGE,"E14"),sQuery(id+"F0.wireOp",EDGE,"E15.1.0"),sQuery(id+"F0.wireOp",EDGE,"E15.1.1"),sQuery(id+"F0.wireOp",EDGE,"E15.2.0"),subQ0])],"isStart":true})],"blendedInto":[makeQuery(id+"F1.opExtrude","CAP_FACE",FACE,{"disambiguationData":[OSD([sQuery(id+"F0.wireOp",EDGE,"E1"),sQuery(id+"F0.wireOp",EDGE,"E2"),sQuery(id+"F0.wireOp",EDGE,"E3"),sQuery(id+"F0.wireOp",EDGE,"E5"),sQuery(id+"F0.wireOp",EDGE,"E6"),sQuery(id+"F0.wireOp",EDGE,"E7.MirrorCS"),sQuery(id+"F0.wireOp",EDGE,"E8.MirrorCS"),sQuery(id+"F0.wireOp",EDGE,"E9.MirrorCS"),sQuery(id+"F0.wireOp",EDGE,"E12.1.0"),sQuery(id+"F0.wireOp",EDGE,"E12.1.1"),sQuery(id+"F0.wireOp",EDGE,"E12.1.2"),sQuery(id+"F0.wireOp",EDGE,"E12.1.3"),sQuery(id+"F0.wireOp",EDGE,"E12.1.4"),sQuery(id+"F0.wireOp",EDGE,"E12.1.5"),subQ1,sQuery(id+"F0.wireOp",EDGE,"E12.2.1"),sQuery(id+"F0.wireOp",EDGE,"E12.2.2"),sQuery(id+"F0.wireOp",EDGE,"E12.2.3"),sQuery(id+"F0.wireOp",EDGE,"E12.2.4"),sQuery(id+"F0.wireOp",EDGE,"E12.2.5"),sQuery(id+"F0.wireOp",EDGE,"E13"),sQuery(id+"F0.wireOp",EDGE,"E14"),sQuery(id+"F0.wireOp",EDGE,"E15.1.0"),sQuery(id+"F0.wireOp",EDGE,"E15.1.1"),sQuery(id+"F0.wireOp",EDGE,"E15.2.0"),subQ0])],"isStart":true})]});}
            var Q40;
            {var subQ0=sQuery(id+"F0.wireOp",EDGE,"E15.2.1");var subQ1=sQuery(id+"F0.wireOp",EDGE,"E6");Q40=makeQuery(id+"F2.opFillet","BLEND_EDGE",EDGE,{"blendedFrom":[makeQuery(id+"F1.opExtrude","SWEPT_EDGE",EDGE,{"disambiguationData":[OSD([subQ1,subQ0])]}),makeQuery(id+"F1.opExtrude","CAP_FACE",FACE,{"disambiguationData":[OSD([sQuery(id+"F0.wireOp",EDGE,"E1"),sQuery(id+"F0.wireOp",EDGE,"E2"),sQuery(id+"F0.wireOp",EDGE,"E3"),sQuery(id+"F0.wireOp",EDGE,"E5"),subQ1,sQuery(id+"F0.wireOp",EDGE,"E7.MirrorCS"),sQuery(id+"F0.wireOp",EDGE,"E8.MirrorCS"),sQuery(id+"F0.wireOp",EDGE,"E9.MirrorCS"),sQuery(id+"F0.wireOp",EDGE,"E12.1.0"),sQuery(id+"F0.wireOp",EDGE,"E12.1.1"),sQuery(id+"F0.wireOp",EDGE,"E12.1.2"),sQuery(id+"F0.wireOp",EDGE,"E12.1.3"),sQuery(id+"F0.wireOp",EDGE,"E12.1.4"),sQuery(id+"F0.wireOp",EDGE,"E12.1.5"),sQuery(id+"F0.wireOp",EDGE,"E12.2.0"),sQuery(id+"F0.wireOp",EDGE,"E12.2.1"),sQuery(id+"F0.wireOp",EDGE,"E12.2.2"),sQuery(id+"F0.wireOp",EDGE,"E12.2.3"),sQuery(id+"F0.wireOp",EDGE,"E12.2.4"),sQuery(id+"F0.wireOp",EDGE,"E12.2.5"),sQuery(id+"F0.wireOp",EDGE,"E13"),sQuery(id+"F0.wireOp",EDGE,"E14"),sQuery(id+"F0.wireOp",EDGE,"E15.1.0"),sQuery(id+"F0.wireOp",EDGE,"E15.1.1"),sQuery(id+"F0.wireOp",EDGE,"E15.2.0"),subQ0])],"isStart":true})],"blendedInto":[makeQuery(id+"F1.opExtrude","CAP_FACE",FACE,{"disambiguationData":[OSD([sQuery(id+"F0.wireOp",EDGE,"E1"),sQuery(id+"F0.wireOp",EDGE,"E2"),sQuery(id+"F0.wireOp",EDGE,"E3"),sQuery(id+"F0.wireOp",EDGE,"E5"),subQ1,sQuery(id+"F0.wireOp",EDGE,"E7.MirrorCS"),sQuery(id+"F0.wireOp",EDGE,"E8.MirrorCS"),sQuery(id+"F0.wireOp",EDGE,"E9.MirrorCS"),sQuery(id+"F0.wireOp",EDGE,"E12.1.0"),sQuery(id+"F0.wireOp",EDGE,"E12.1.1"),sQuery(id+"F0.wireOp",EDGE,"E12.1.2"),sQuery(id+"F0.wireOp",EDGE,"E12.1.3"),sQuery(id+"F0.wireOp",EDGE,"E12.1.4"),sQuery(id+"F0.wireOp",EDGE,"E12.1.5"),sQuery(id+"F0.wireOp",EDGE,"E12.2.0"),sQuery(id+"F0.wireOp",EDGE,"E12.2.1"),sQuery(id+"F0.wireOp",EDGE,"E12.2.2"),sQuery(id+"F0.wireOp",EDGE,"E12.2.3"),sQuery(id+"F0.wireOp",EDGE,"E12.2.4"),sQuery(id+"F0.wireOp",EDGE,"E12.2.5"),sQuery(id+"F0.wireOp",EDGE,"E13"),sQuery(id+"F0.wireOp",EDGE,"E14"),sQuery(id+"F0.wireOp",EDGE,"E15.1.0"),sQuery(id+"F0.wireOp",EDGE,"E15.1.1"),sQuery(id+"F0.wireOp",EDGE,"E15.2.0"),subQ0])],"isStart":true})]});}
            var Q41;
            {var subQ0=sQuery(id+"F0.wireOp",EDGE,"E15.1.0");var subQ1=sQuery(id+"F0.wireOp",EDGE,"E12.1.5");Q41=makeQuery(id+"F2.opFillet","BLEND_EDGE",EDGE,{"blendedFrom":[makeQuery(id+"F1.opExtrude","SWEPT_EDGE",EDGE,{"disambiguationData":[OSD([subQ1,subQ0])]}),makeQuery(id+"F1.opExtrude","CAP_FACE",FACE,{"disambiguationData":[OSD([sQuery(id+"F0.wireOp",EDGE,"E1"),sQuery(id+"F0.wireOp",EDGE,"E2"),sQuery(id+"F0.wireOp",EDGE,"E3"),sQuery(id+"F0.wireOp",EDGE,"E5"),sQuery(id+"F0.wireOp",EDGE,"E6"),sQuery(id+"F0.wireOp",EDGE,"E7.MirrorCS"),sQuery(id+"F0.wireOp",EDGE,"E8.MirrorCS"),sQuery(id+"F0.wireOp",EDGE,"E9.MirrorCS"),sQuery(id+"F0.wireOp",EDGE,"E12.1.0"),sQuery(id+"F0.wireOp",EDGE,"E12.1.1"),sQuery(id+"F0.wireOp",EDGE,"E12.1.2"),sQuery(id+"F0.wireOp",EDGE,"E12.1.3"),sQuery(id+"F0.wireOp",EDGE,"E12.1.4"),subQ1,sQuery(id+"F0.wireOp",EDGE,"E12.2.0"),sQuery(id+"F0.wireOp",EDGE,"E12.2.1"),sQuery(id+"F0.wireOp",EDGE,"E12.2.2"),sQuery(id+"F0.wireOp",EDGE,"E12.2.3"),sQuery(id+"F0.wireOp",EDGE,"E12.2.4"),sQuery(id+"F0.wireOp",EDGE,"E12.2.5"),sQuery(id+"F0.wireOp",EDGE,"E13"),sQuery(id+"F0.wireOp",EDGE,"E14"),subQ0,sQuery(id+"F0.wireOp",EDGE,"E15.1.1"),sQuery(id+"F0.wireOp",EDGE,"E15.2.0"),sQuery(id+"F0.wireOp",EDGE,"E15.2.1")])],"isStart":true})],"blendedInto":[makeQuery(id+"F1.opExtrude","CAP_FACE",FACE,{"disambiguationData":[OSD([sQuery(id+"F0.wireOp",EDGE,"E1"),sQuery(id+"F0.wireOp",EDGE,"E2"),sQuery(id+"F0.wireOp",EDGE,"E3"),sQuery(id+"F0.wireOp",EDGE,"E5"),sQuery(id+"F0.wireOp",EDGE,"E6"),sQuery(id+"F0.wireOp",EDGE,"E7.MirrorCS"),sQuery(id+"F0.wireOp",EDGE,"E8.MirrorCS"),sQuery(id+"F0.wireOp",EDGE,"E9.MirrorCS"),sQuery(id+"F0.wireOp",EDGE,"E12.1.0"),sQuery(id+"F0.wireOp",EDGE,"E12.1.1"),sQuery(id+"F0.wireOp",EDGE,"E12.1.2"),sQuery(id+"F0.wireOp",EDGE,"E12.1.3"),sQuery(id+"F0.wireOp",EDGE,"E12.1.4"),subQ1,sQuery(id+"F0.wireOp",EDGE,"E12.2.0"),sQuery(id+"F0.wireOp",EDGE,"E12.2.1"),sQuery(id+"F0.wireOp",EDGE,"E12.2.2"),sQuery(id+"F0.wireOp",EDGE,"E12.2.3"),sQuery(id+"F0.wireOp",EDGE,"E12.2.4"),sQuery(id+"F0.wireOp",EDGE,"E12.2.5"),sQuery(id+"F0.wireOp",EDGE,"E13"),sQuery(id+"F0.wireOp",EDGE,"E14"),subQ0,sQuery(id+"F0.wireOp",EDGE,"E15.1.1"),sQuery(id+"F0.wireOp",EDGE,"E15.2.0"),sQuery(id+"F0.wireOp",EDGE,"E15.2.1")])],"isStart":true})]});}
            var Q42;
            {var subQ0=sQuery(id+"F0.wireOp",EDGE,"E15.1.0");var subQ1=sQuery(id+"F0.wireOp",EDGE,"E6");Q42=makeQuery(id+"F2.opFillet","BLEND_EDGE",EDGE,{"blendedFrom":[makeQuery(id+"F1.opExtrude","SWEPT_EDGE",EDGE,{"disambiguationData":[OSD([subQ1,subQ0])]}),makeQuery(id+"F1.opExtrude","CAP_FACE",FACE,{"disambiguationData":[OSD([sQuery(id+"F0.wireOp",EDGE,"E1"),sQuery(id+"F0.wireOp",EDGE,"E2"),sQuery(id+"F0.wireOp",EDGE,"E3"),sQuery(id+"F0.wireOp",EDGE,"E5"),subQ1,sQuery(id+"F0.wireOp",EDGE,"E7.MirrorCS"),sQuery(id+"F0.wireOp",EDGE,"E8.MirrorCS"),sQuery(id+"F0.wireOp",EDGE,"E9.MirrorCS"),sQuery(id+"F0.wireOp",EDGE,"E12.1.0"),sQuery(id+"F0.wireOp",EDGE,"E12.1.1"),sQuery(id+"F0.wireOp",EDGE,"E12.1.2"),sQuery(id+"F0.wireOp",EDGE,"E12.1.3"),sQuery(id+"F0.wireOp",EDGE,"E12.1.4"),sQuery(id+"F0.wireOp",EDGE,"E12.1.5"),sQuery(id+"F0.wireOp",EDGE,"E12.2.0"),sQuery(id+"F0.wireOp",EDGE,"E12.2.1"),sQuery(id+"F0.wireOp",EDGE,"E12.2.2"),sQuery(id+"F0.wireOp",EDGE,"E12.2.3"),sQuery(id+"F0.wireOp",EDGE,"E12.2.4"),sQuery(id+"F0.wireOp",EDGE,"E12.2.5"),sQuery(id+"F0.wireOp",EDGE,"E13"),sQuery(id+"F0.wireOp",EDGE,"E14"),subQ0,sQuery(id+"F0.wireOp",EDGE,"E15.1.1"),sQuery(id+"F0.wireOp",EDGE,"E15.2.0"),sQuery(id+"F0.wireOp",EDGE,"E15.2.1")])],"isStart":true})],"blendedInto":[makeQuery(id+"F1.opExtrude","CAP_FACE",FACE,{"disambiguationData":[OSD([sQuery(id+"F0.wireOp",EDGE,"E1"),sQuery(id+"F0.wireOp",EDGE,"E2"),sQuery(id+"F0.wireOp",EDGE,"E3"),sQuery(id+"F0.wireOp",EDGE,"E5"),subQ1,sQuery(id+"F0.wireOp",EDGE,"E7.MirrorCS"),sQuery(id+"F0.wireOp",EDGE,"E8.MirrorCS"),sQuery(id+"F0.wireOp",EDGE,"E9.MirrorCS"),sQuery(id+"F0.wireOp",EDGE,"E12.1.0"),sQuery(id+"F0.wireOp",EDGE,"E12.1.1"),sQuery(id+"F0.wireOp",EDGE,"E12.1.2"),sQuery(id+"F0.wireOp",EDGE,"E12.1.3"),sQuery(id+"F0.wireOp",EDGE,"E12.1.4"),sQuery(id+"F0.wireOp",EDGE,"E12.1.5"),sQuery(id+"F0.wireOp",EDGE,"E12.2.0"),sQuery(id+"F0.wireOp",EDGE,"E12.2.1"),sQuery(id+"F0.wireOp",EDGE,"E12.2.2"),sQuery(id+"F0.wireOp",EDGE,"E12.2.3"),sQuery(id+"F0.wireOp",EDGE,"E12.2.4"),sQuery(id+"F0.wireOp",EDGE,"E12.2.5"),sQuery(id+"F0.wireOp",EDGE,"E13"),sQuery(id+"F0.wireOp",EDGE,"E14"),subQ0,sQuery(id+"F0.wireOp",EDGE,"E15.1.1"),sQuery(id+"F0.wireOp",EDGE,"E15.2.0"),sQuery(id+"F0.wireOp",EDGE,"E15.2.1")])],"isStart":true})]});}
            var Q43;
            Q43=makeQuery(id+"F1.opExtrude","CAP_EDGE",EDGE,{"disambiguationData":[OSD([sQuery(id+"F0.wireOp",EDGE,"E12.1.0")])],"isStart":false});
            fillet(context, id + "F3", {"entities" : qUnion([Q0, Q1, Q2, Q3, Q4, Q5, Q6, Q7, Q8, Q9, Q10, Q11, Q12, Q13, Q14, Q15, Q16, Q17, Q18, Q19, Q20, Q21, Q22, Q23, Q24, Q25, Q26, Q27, Q28, Q29, Q30, Q31, Q32, Q33, Q34, Q35, Q36, Q37, Q38, Q39, Q40, Q41, Q42, Q43]), "radius" : 4 * mm, "tangentPropagation" : true, "allowEdgeOverflow" : false});
        }
        {
            var Q0;
            Q0=makeQuery(id+"F1.opExtrude","SWEPT_FACE",FACE,{"disambiguationData":[OSD([sQuery(id+"F0.wireOp",EDGE,"E12.1.4")])]});
            chamfer(context, id + "F4", {"entities" : qUnion([Q0]), "width" : 2.5 * mm, "tangentPropagation" : true});
        }
    });
